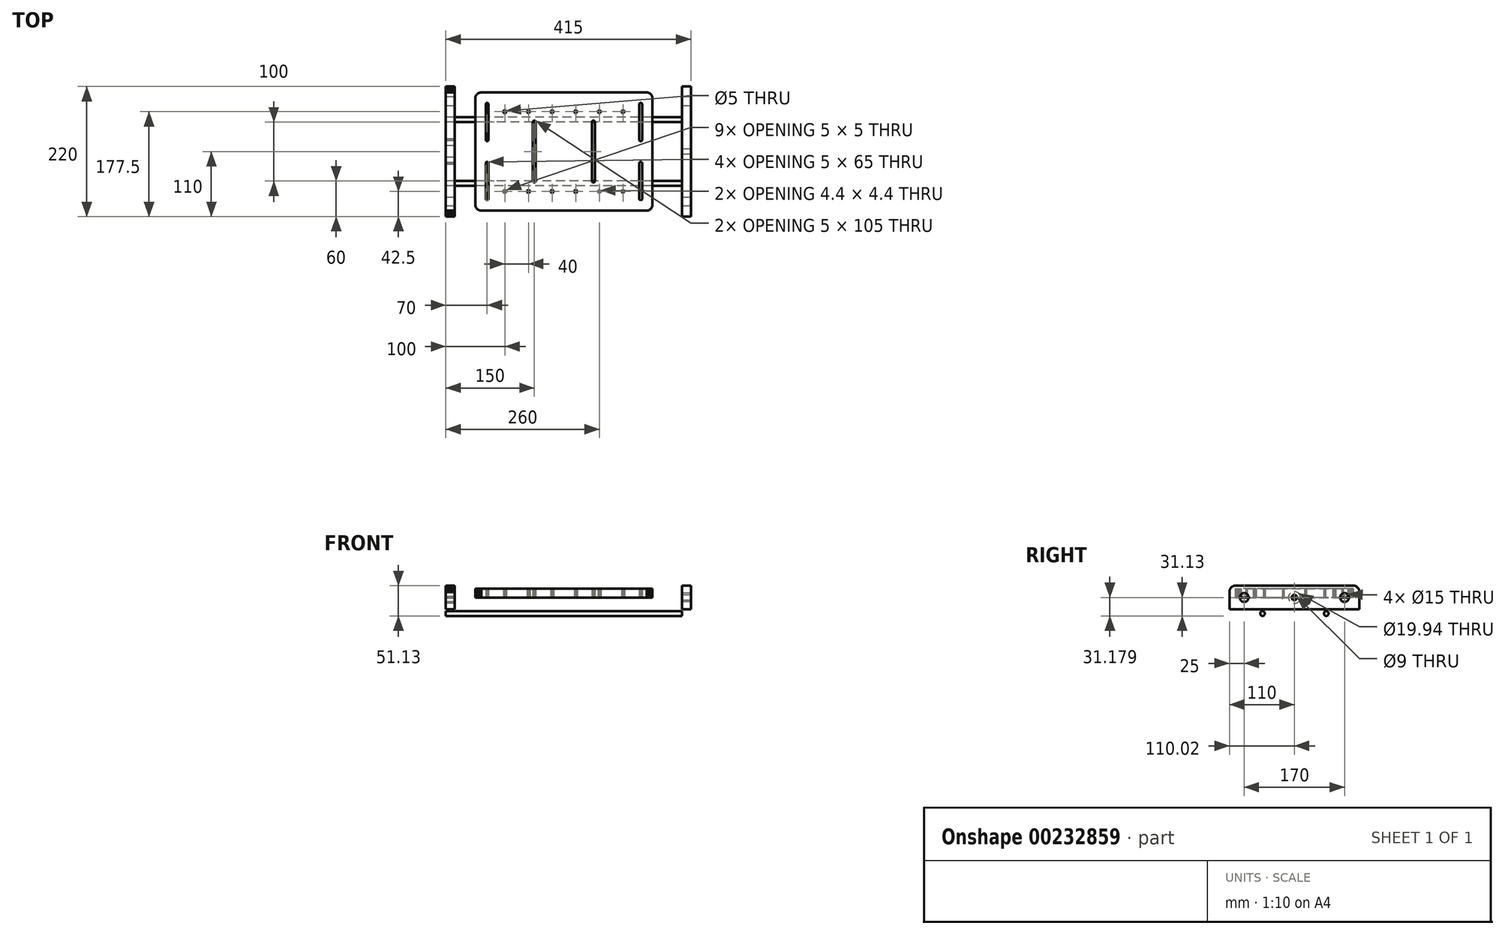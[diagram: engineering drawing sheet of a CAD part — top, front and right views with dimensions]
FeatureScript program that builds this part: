
annotation { "Feature Type Name" : "Feature", "Feature Type Description" : "" }
export const myFeature = defineFeature(function(context is Context, id is Id, definition is map)
    precondition{}
    {
        {
            var Q0;
            Q0=qCreatedBy(makeId("Top.planeOp"),FACE);
            var sketch = newSketch(context, id + "F0", { "sketchPlane" : qUnion([Q0])});
            skLineSegment(sketch, "E0", {"start": v(98.75, 69.67) * mm, "end": v(99.35, 69.91) * mm});
            skLineSegment(sketch, "E1", {"start": v(99.35, 69.91) * mm, "end": v(100, 70) * mm});
            skLineSegment(sketch, "E2", {"start": v(100, 70) * mm, "end": v(100.65, 69.91) * mm});
            skLineSegment(sketch, "E3", {"start": v(100.65, 69.91) * mm, "end": v(101.25, 69.67) * mm});
            skLineSegment(sketch, "E4", {"start": v(101.25, 69.67) * mm, "end": v(101.77, 69.27) * mm});
            skLineSegment(sketch, "E5", {"start": v(101.77, 69.27) * mm, "end": v(102.17, 68.75) * mm});
            skLineSegment(sketch, "E6", {"start": v(102.17, 68.75) * mm, "end": v(102.41, 68.15) * mm});
            skLineSegment(sketch, "E7", {"start": v(102.41, 68.15) * mm, "end": v(102.5, 67.5) * mm});
            skLineSegment(sketch, "E8", {"start": v(102.5, 67.5) * mm, "end": v(102.41, 66.85) * mm});
            skLineSegment(sketch, "E9", {"start": v(102.41, 66.85) * mm, "end": v(102.17, 66.25) * mm});
            skLineSegment(sketch, "E10", {"start": v(102.17, 66.25) * mm, "end": v(101.77, 65.73) * mm});
            skLineSegment(sketch, "E11", {"start": v(101.77, 65.73) * mm, "end": v(101.25, 65.33) * mm});
            skLineSegment(sketch, "E12", {"start": v(101.25, 65.33) * mm, "end": v(100.65, 65.09) * mm});
            skLineSegment(sketch, "E13", {"start": v(100.65, 65.09) * mm, "end": v(100, 65) * mm});
            skLineSegment(sketch, "E14", {"start": v(100, 65) * mm, "end": v(99.35, 65.09) * mm});
            skLineSegment(sketch, "E15", {"start": v(99.35, 65.09) * mm, "end": v(98.75, 65.33) * mm});
            skLineSegment(sketch, "E16", {"start": v(98.75, 65.33) * mm, "end": v(98.23, 65.73) * mm});
            skLineSegment(sketch, "E17", {"start": v(98.23, 65.73) * mm, "end": v(97.83, 66.25) * mm});
            skLineSegment(sketch, "E18", {"start": v(97.83, 66.25) * mm, "end": v(97.59, 66.85) * mm});
            skLineSegment(sketch, "E19", {"start": v(97.59, 66.85) * mm, "end": v(97.5, 67.5) * mm});
            skLineSegment(sketch, "E20", {"start": v(97.5, 67.5) * mm, "end": v(97.59, 68.15) * mm});
            skLineSegment(sketch, "E21", {"start": v(97.59, 68.15) * mm, "end": v(97.83, 68.75) * mm});
            skLineSegment(sketch, "E22", {"start": v(97.83, 68.75) * mm, "end": v(98.23, 69.27) * mm});
            skLineSegment(sketch, "E23", {"start": v(98.23, 69.27) * mm, "end": v(98.75, 69.67) * mm});
            skLineSegment(sketch, "E24", {"start": v(98.55, 67.89) * mm, "end": v(98.5, 67.5) * mm});
            skLineSegment(sketch, "E25", {"start": v(98.5, 67.5) * mm, "end": v(98.55, 67.11) * mm});
            skLineSegment(sketch, "E26", {"start": v(98.55, 67.11) * mm, "end": v(98.7, 66.75) * mm});
            skLineSegment(sketch, "E27", {"start": v(98.7, 66.75) * mm, "end": v(98.94, 66.44) * mm});
            skLineSegment(sketch, "E28", {"start": v(98.94, 66.44) * mm, "end": v(99.25, 66.2) * mm});
            skLineSegment(sketch, "E29", {"start": v(99.25, 66.2) * mm, "end": v(99.61, 66.05) * mm});
            skLineSegment(sketch, "E30", {"start": v(99.61, 66.05) * mm, "end": v(100, 66) * mm});
            skLineSegment(sketch, "E31", {"start": v(100, 66) * mm, "end": v(100.39, 66.05) * mm});
            skLineSegment(sketch, "E32", {"start": v(100.39, 66.05) * mm, "end": v(100.75, 66.2) * mm});
            skLineSegment(sketch, "E33", {"start": v(100.75, 66.2) * mm, "end": v(101.06, 66.44) * mm});
            skLineSegment(sketch, "E34", {"start": v(101.06, 66.44) * mm, "end": v(101.3, 66.75) * mm});
            skLineSegment(sketch, "E35", {"start": v(101.3, 66.75) * mm, "end": v(101.45, 67.11) * mm});
            skLineSegment(sketch, "E36", {"start": v(101.45, 67.11) * mm, "end": v(101.5, 67.5) * mm});
            skLineSegment(sketch, "E37", {"start": v(101.5, 67.5) * mm, "end": v(101.45, 67.89) * mm});
            skLineSegment(sketch, "E38", {"start": v(101.45, 67.89) * mm, "end": v(101.3, 68.25) * mm});
            skLineSegment(sketch, "E39", {"start": v(101.3, 68.25) * mm, "end": v(101.06, 68.56) * mm});
            skLineSegment(sketch, "E40", {"start": v(101.06, 68.56) * mm, "end": v(100.75, 68.8) * mm});
            skLineSegment(sketch, "E41", {"start": v(100.75, 68.8) * mm, "end": v(100.39, 68.95) * mm});
            skLineSegment(sketch, "E42", {"start": v(100.39, 68.95) * mm, "end": v(100, 69) * mm});
            skLineSegment(sketch, "E43", {"start": v(100, 69) * mm, "end": v(99.61, 68.95) * mm});
            skLineSegment(sketch, "E44", {"start": v(99.61, 68.95) * mm, "end": v(99.25, 68.8) * mm});
            skLineSegment(sketch, "E45", {"start": v(99.25, 68.8) * mm, "end": v(98.94, 68.56) * mm});
            skLineSegment(sketch, "E46", {"start": v(98.94, 68.56) * mm, "end": v(98.7, 68.25) * mm});
            skLineSegment(sketch, "E47", {"start": v(98.7, 68.25) * mm, "end": v(98.55, 67.89) * mm});
            skLineSegment(sketch, "E48", {"start": v(-101.25, -69.67) * mm, "end": v(-101.77, -69.27) * mm});
            skLineSegment(sketch, "E49", {"start": v(-101.77, -69.27) * mm, "end": v(-102.17, -68.75) * mm});
            skLineSegment(sketch, "E50", {"start": v(-102.17, -68.75) * mm, "end": v(-102.41, -68.15) * mm});
            skLineSegment(sketch, "E51", {"start": v(-102.41, -68.15) * mm, "end": v(-102.5, -67.5) * mm});
            skLineSegment(sketch, "E52", {"start": v(-102.5, -67.5) * mm, "end": v(-102.41, -66.85) * mm});
            skLineSegment(sketch, "E53", {"start": v(-102.41, -66.85) * mm, "end": v(-102.17, -66.25) * mm});
            skLineSegment(sketch, "E54", {"start": v(-102.17, -66.25) * mm, "end": v(-101.77, -65.73) * mm});
            skLineSegment(sketch, "E55", {"start": v(-101.77, -65.73) * mm, "end": v(-101.25, -65.33) * mm});
            skLineSegment(sketch, "E56", {"start": v(-101.25, -65.33) * mm, "end": v(-100.65, -65.09) * mm});
            skLineSegment(sketch, "E57", {"start": v(-100.65, -65.09) * mm, "end": v(-100, -65) * mm});
            skLineSegment(sketch, "E58", {"start": v(-100, -65) * mm, "end": v(-99.35, -65.09) * mm});
            skLineSegment(sketch, "E59", {"start": v(-99.35, -65.09) * mm, "end": v(-98.75, -65.33) * mm});
            skLineSegment(sketch, "E60", {"start": v(-98.75, -65.33) * mm, "end": v(-98.23, -65.73) * mm});
            skLineSegment(sketch, "E61", {"start": v(-98.23, -65.73) * mm, "end": v(-97.83, -66.25) * mm});
            skLineSegment(sketch, "E62", {"start": v(-97.83, -66.25) * mm, "end": v(-97.59, -66.85) * mm});
            skLineSegment(sketch, "E63", {"start": v(-97.59, -66.85) * mm, "end": v(-97.5, -67.5) * mm});
            skLineSegment(sketch, "E64", {"start": v(-97.5, -67.5) * mm, "end": v(-97.59, -68.15) * mm});
            skLineSegment(sketch, "E65", {"start": v(-97.59, -68.15) * mm, "end": v(-97.83, -68.75) * mm});
            skLineSegment(sketch, "E66", {"start": v(-97.83, -68.75) * mm, "end": v(-98.23, -69.27) * mm});
            skLineSegment(sketch, "E67", {"start": v(-98.23, -69.27) * mm, "end": v(-98.75, -69.67) * mm});
            skLineSegment(sketch, "E68", {"start": v(-98.75, -69.67) * mm, "end": v(-99.35, -69.91) * mm});
            skLineSegment(sketch, "E69", {"start": v(-99.35, -69.91) * mm, "end": v(-100, -70) * mm});
            skLineSegment(sketch, "E70", {"start": v(-100, -70) * mm, "end": v(-100.65, -69.91) * mm});
            skLineSegment(sketch, "E71", {"start": v(-100.65, -69.91) * mm, "end": v(-101.25, -69.67) * mm});
            skLineSegment(sketch, "E72", {"start": v(-101.45, -67.89) * mm, "end": v(-101.3, -68.25) * mm});
            skLineSegment(sketch, "E73", {"start": v(-101.3, -68.25) * mm, "end": v(-101.06, -68.56) * mm});
            skLineSegment(sketch, "E74", {"start": v(-101.06, -68.56) * mm, "end": v(-100.75, -68.8) * mm});
            skLineSegment(sketch, "E75", {"start": v(-100.75, -68.8) * mm, "end": v(-100.39, -68.95) * mm});
            skLineSegment(sketch, "E76", {"start": v(-100.39, -68.95) * mm, "end": v(-100, -69) * mm});
            skLineSegment(sketch, "E77", {"start": v(-100, -69) * mm, "end": v(-99.61, -68.95) * mm});
            skLineSegment(sketch, "E78", {"start": v(-99.61, -68.95) * mm, "end": v(-99.25, -68.8) * mm});
            skLineSegment(sketch, "E79", {"start": v(-99.25, -68.8) * mm, "end": v(-98.94, -68.56) * mm});
            skLineSegment(sketch, "E80", {"start": v(-98.94, -68.56) * mm, "end": v(-98.7, -68.25) * mm});
            skLineSegment(sketch, "E81", {"start": v(-98.7, -68.25) * mm, "end": v(-98.55, -67.89) * mm});
            skLineSegment(sketch, "E82", {"start": v(-98.55, -67.89) * mm, "end": v(-98.5, -67.5) * mm});
            skLineSegment(sketch, "E83", {"start": v(-98.5, -67.5) * mm, "end": v(-98.55, -67.11) * mm});
            skLineSegment(sketch, "E84", {"start": v(-98.55, -67.11) * mm, "end": v(-98.7, -66.75) * mm});
            skLineSegment(sketch, "E85", {"start": v(-98.7, -66.75) * mm, "end": v(-98.94, -66.44) * mm});
            skLineSegment(sketch, "E86", {"start": v(-98.94, -66.44) * mm, "end": v(-99.25, -66.2) * mm});
            skLineSegment(sketch, "E87", {"start": v(-99.25, -66.2) * mm, "end": v(-99.61, -66.05) * mm});
            skLineSegment(sketch, "E88", {"start": v(-99.61, -66.05) * mm, "end": v(-100, -66) * mm});
            skLineSegment(sketch, "E89", {"start": v(-100, -66) * mm, "end": v(-100.39, -66.05) * mm});
            skLineSegment(sketch, "E90", {"start": v(-100.39, -66.05) * mm, "end": v(-100.75, -66.2) * mm});
            skLineSegment(sketch, "E91", {"start": v(-100.75, -66.2) * mm, "end": v(-101.06, -66.44) * mm});
            skLineSegment(sketch, "E92", {"start": v(-101.06, -66.44) * mm, "end": v(-101.3, -66.75) * mm});
            skLineSegment(sketch, "E93", {"start": v(-101.3, -66.75) * mm, "end": v(-101.45, -67.11) * mm});
            skLineSegment(sketch, "E94", {"start": v(-101.45, -67.11) * mm, "end": v(-101.5, -67.5) * mm});
            skLineSegment(sketch, "E95", {"start": v(-101.5, -67.5) * mm, "end": v(-101.45, -67.89) * mm});
            skLineSegment(sketch, "E96", {"start": v(60, -65.3) * mm, "end": v(60.57, -65.37) * mm});
            skLineSegment(sketch, "E97", {"start": v(60.57, -65.37) * mm, "end": v(61.1, -65.6) * mm});
            skLineSegment(sketch, "E98", {"start": v(61.1, -65.6) * mm, "end": v(61.56, -65.94) * mm});
            skLineSegment(sketch, "E99", {"start": v(61.56, -65.94) * mm, "end": v(61.9, -66.4) * mm});
            skLineSegment(sketch, "E100", {"start": v(61.9, -66.4) * mm, "end": v(62.13, -66.93) * mm});
            skLineSegment(sketch, "E101", {"start": v(62.13, -66.93) * mm, "end": v(62.2, -67.5) * mm});
            skLineSegment(sketch, "E102", {"start": v(62.2, -67.5) * mm, "end": v(62.13, -68.07) * mm});
            skLineSegment(sketch, "E103", {"start": v(62.13, -68.07) * mm, "end": v(61.9, -68.6) * mm});
            skLineSegment(sketch, "E104", {"start": v(61.9, -68.6) * mm, "end": v(61.56, -69.06) * mm});
            skLineSegment(sketch, "E105", {"start": v(61.56, -69.06) * mm, "end": v(61.1, -69.4) * mm});
            skLineSegment(sketch, "E106", {"start": v(61.1, -69.4) * mm, "end": v(60.57, -69.63) * mm});
            skLineSegment(sketch, "E107", {"start": v(60.57, -69.63) * mm, "end": v(60, -69.7) * mm});
            skLineSegment(sketch, "E108", {"start": v(60, -69.7) * mm, "end": v(59.43, -69.63) * mm});
            skLineSegment(sketch, "E109", {"start": v(59.43, -69.63) * mm, "end": v(58.9, -69.4) * mm});
            skLineSegment(sketch, "E110", {"start": v(58.9, -69.4) * mm, "end": v(58.44, -69.06) * mm});
            skLineSegment(sketch, "E111", {"start": v(58.44, -69.06) * mm, "end": v(58.1, -68.6) * mm});
            skLineSegment(sketch, "E112", {"start": v(58.1, -68.6) * mm, "end": v(57.87, -68.07) * mm});
            skLineSegment(sketch, "E113", {"start": v(57.87, -68.07) * mm, "end": v(57.8, -67.5) * mm});
            skLineSegment(sketch, "E114", {"start": v(57.8, -67.5) * mm, "end": v(57.87, -66.93) * mm});
            skLineSegment(sketch, "E115", {"start": v(57.87, -66.93) * mm, "end": v(58.1, -66.4) * mm});
            skLineSegment(sketch, "E116", {"start": v(58.1, -66.4) * mm, "end": v(58.44, -65.94) * mm});
            skLineSegment(sketch, "E117", {"start": v(58.44, -65.94) * mm, "end": v(58.9, -65.6) * mm});
            skLineSegment(sketch, "E118", {"start": v(58.9, -65.6) * mm, "end": v(59.43, -65.37) * mm});
            skLineSegment(sketch, "E119", {"start": v(59.43, -65.37) * mm, "end": v(60, -65.3) * mm});
            skLineSegment(sketch, "E120", {"start": v(61.3, -66.75) * mm, "end": v(61.06, -66.44) * mm});
            skLineSegment(sketch, "E121", {"start": v(61.06, -66.44) * mm, "end": v(60.75, -66.2) * mm});
            skLineSegment(sketch, "E122", {"start": v(60.75, -66.2) * mm, "end": v(60.39, -66.05) * mm});
            skLineSegment(sketch, "E123", {"start": v(60.39, -66.05) * mm, "end": v(60, -66) * mm});
            skLineSegment(sketch, "E124", {"start": v(60, -66) * mm, "end": v(59.61, -66.05) * mm});
            skLineSegment(sketch, "E125", {"start": v(59.61, -66.05) * mm, "end": v(59.25, -66.2) * mm});
            skLineSegment(sketch, "E126", {"start": v(59.25, -66.2) * mm, "end": v(58.94, -66.44) * mm});
            skLineSegment(sketch, "E127", {"start": v(58.94, -66.44) * mm, "end": v(58.7, -66.75) * mm});
            skLineSegment(sketch, "E128", {"start": v(58.7, -66.75) * mm, "end": v(58.55, -67.11) * mm});
            skLineSegment(sketch, "E129", {"start": v(58.55, -67.11) * mm, "end": v(58.5, -67.5) * mm});
            skLineSegment(sketch, "E130", {"start": v(58.5, -67.5) * mm, "end": v(58.55, -67.89) * mm});
            skLineSegment(sketch, "E131", {"start": v(58.55, -67.89) * mm, "end": v(58.7, -68.25) * mm});
            skLineSegment(sketch, "E132", {"start": v(58.7, -68.25) * mm, "end": v(58.94, -68.56) * mm});
            skLineSegment(sketch, "E133", {"start": v(58.94, -68.56) * mm, "end": v(59.25, -68.8) * mm});
            skLineSegment(sketch, "E134", {"start": v(59.25, -68.8) * mm, "end": v(59.61, -68.95) * mm});
            skLineSegment(sketch, "E135", {"start": v(59.61, -68.95) * mm, "end": v(60, -69) * mm});
            skLineSegment(sketch, "E136", {"start": v(60, -69) * mm, "end": v(60.39, -68.95) * mm});
            skLineSegment(sketch, "E137", {"start": v(60.39, -68.95) * mm, "end": v(60.75, -68.8) * mm});
            skLineSegment(sketch, "E138", {"start": v(60.75, -68.8) * mm, "end": v(61.06, -68.56) * mm});
            skLineSegment(sketch, "E139", {"start": v(61.06, -68.56) * mm, "end": v(61.3, -68.25) * mm});
            skLineSegment(sketch, "E140", {"start": v(61.3, -68.25) * mm, "end": v(61.45, -67.89) * mm});
            skLineSegment(sketch, "E141", {"start": v(61.45, -67.89) * mm, "end": v(61.5, -67.5) * mm});
            skLineSegment(sketch, "E142", {"start": v(61.5, -67.5) * mm, "end": v(61.45, -67.11) * mm});
            skLineSegment(sketch, "E143", {"start": v(61.45, -67.11) * mm, "end": v(61.3, -66.75) * mm});
            skLineSegment(sketch, "E144", {"start": v(-18.23, -65.73) * mm, "end": v(-17.83, -66.25) * mm});
            skLineSegment(sketch, "E145", {"start": v(-17.83, -66.25) * mm, "end": v(-17.59, -66.85) * mm});
            skLineSegment(sketch, "E146", {"start": v(-17.59, -66.85) * mm, "end": v(-17.5, -67.5) * mm});
            skLineSegment(sketch, "E147", {"start": v(-17.5, -67.5) * mm, "end": v(-17.59, -68.15) * mm});
            skLineSegment(sketch, "E148", {"start": v(-17.59, -68.15) * mm, "end": v(-17.83, -68.75) * mm});
            skLineSegment(sketch, "E149", {"start": v(-17.83, -68.75) * mm, "end": v(-18.23, -69.27) * mm});
            skLineSegment(sketch, "E150", {"start": v(-18.23, -69.27) * mm, "end": v(-18.75, -69.67) * mm});
            skLineSegment(sketch, "E151", {"start": v(-18.75, -69.67) * mm, "end": v(-19.35, -69.91) * mm});
            skLineSegment(sketch, "E152", {"start": v(-19.35, -69.91) * mm, "end": v(-20, -70) * mm});
            skLineSegment(sketch, "E153", {"start": v(-20, -70) * mm, "end": v(-20.65, -69.91) * mm});
            skLineSegment(sketch, "E154", {"start": v(-20.65, -69.91) * mm, "end": v(-21.25, -69.67) * mm});
            skLineSegment(sketch, "E155", {"start": v(-21.25, -69.67) * mm, "end": v(-21.77, -69.27) * mm});
            skLineSegment(sketch, "E156", {"start": v(-21.77, -69.27) * mm, "end": v(-22.17, -68.75) * mm});
            skLineSegment(sketch, "E157", {"start": v(-22.17, -68.75) * mm, "end": v(-22.41, -68.15) * mm});
            skLineSegment(sketch, "E158", {"start": v(-22.41, -68.15) * mm, "end": v(-22.5, -67.5) * mm});
            skLineSegment(sketch, "E159", {"start": v(-22.5, -67.5) * mm, "end": v(-22.41, -66.85) * mm});
            skLineSegment(sketch, "E160", {"start": v(-22.41, -66.85) * mm, "end": v(-22.17, -66.25) * mm});
            skLineSegment(sketch, "E161", {"start": v(-22.17, -66.25) * mm, "end": v(-21.77, -65.73) * mm});
            skLineSegment(sketch, "E162", {"start": v(-21.77, -65.73) * mm, "end": v(-21.25, -65.33) * mm});
            skLineSegment(sketch, "E163", {"start": v(-21.25, -65.33) * mm, "end": v(-20.65, -65.09) * mm});
            skLineSegment(sketch, "E164", {"start": v(-20.65, -65.09) * mm, "end": v(-20, -65) * mm});
            skLineSegment(sketch, "E165", {"start": v(-20, -65) * mm, "end": v(-19.35, -65.09) * mm});
            skLineSegment(sketch, "E166", {"start": v(-19.35, -65.09) * mm, "end": v(-18.75, -65.33) * mm});
            skLineSegment(sketch, "E167", {"start": v(-18.75, -65.33) * mm, "end": v(-18.23, -65.73) * mm});
            skLineSegment(sketch, "E168", {"start": v(-20.39, -68.95) * mm, "end": v(-20, -69) * mm});
            skLineSegment(sketch, "E169", {"start": v(-20, -69) * mm, "end": v(-19.61, -68.95) * mm});
            skLineSegment(sketch, "E170", {"start": v(-19.61, -68.95) * mm, "end": v(-19.25, -68.8) * mm});
            skLineSegment(sketch, "E171", {"start": v(-19.25, -68.8) * mm, "end": v(-18.94, -68.56) * mm});
            skLineSegment(sketch, "E172", {"start": v(-18.94, -68.56) * mm, "end": v(-18.7, -68.25) * mm});
            skLineSegment(sketch, "E173", {"start": v(-18.7, -68.25) * mm, "end": v(-18.55, -67.89) * mm});
            skLineSegment(sketch, "E174", {"start": v(-18.55, -67.89) * mm, "end": v(-18.5, -67.5) * mm});
            skLineSegment(sketch, "E175", {"start": v(-18.5, -67.5) * mm, "end": v(-18.55, -67.11) * mm});
            skLineSegment(sketch, "E176", {"start": v(-18.55, -67.11) * mm, "end": v(-18.7, -66.75) * mm});
            skLineSegment(sketch, "E177", {"start": v(-18.7, -66.75) * mm, "end": v(-18.94, -66.44) * mm});
            skLineSegment(sketch, "E178", {"start": v(-18.94, -66.44) * mm, "end": v(-19.25, -66.2) * mm});
            skLineSegment(sketch, "E179", {"start": v(-19.25, -66.2) * mm, "end": v(-19.61, -66.05) * mm});
            skLineSegment(sketch, "E180", {"start": v(-19.61, -66.05) * mm, "end": v(-20, -66) * mm});
            skLineSegment(sketch, "E181", {"start": v(-20, -66) * mm, "end": v(-20.39, -66.05) * mm});
            skLineSegment(sketch, "E182", {"start": v(-20.39, -66.05) * mm, "end": v(-20.75, -66.2) * mm});
            skLineSegment(sketch, "E183", {"start": v(-20.75, -66.2) * mm, "end": v(-21.06, -66.44) * mm});
            skLineSegment(sketch, "E184", {"start": v(-21.06, -66.44) * mm, "end": v(-21.3, -66.75) * mm});
            skLineSegment(sketch, "E185", {"start": v(-21.3, -66.75) * mm, "end": v(-21.45, -67.11) * mm});
            skLineSegment(sketch, "E186", {"start": v(-21.45, -67.11) * mm, "end": v(-21.5, -67.5) * mm});
            skLineSegment(sketch, "E187", {"start": v(-21.5, -67.5) * mm, "end": v(-21.45, -67.89) * mm});
            skLineSegment(sketch, "E188", {"start": v(-21.45, -67.89) * mm, "end": v(-21.3, -68.25) * mm});
            skLineSegment(sketch, "E189", {"start": v(-21.3, -68.25) * mm, "end": v(-21.06, -68.56) * mm});
            skLineSegment(sketch, "E190", {"start": v(-21.06, -68.56) * mm, "end": v(-20.75, -68.8) * mm});
            skLineSegment(sketch, "E191", {"start": v(-20.75, -68.8) * mm, "end": v(-20.39, -68.95) * mm});
            skLineSegment(sketch, "E192", {"start": v(21.25, 65.33) * mm, "end": v(20.65, 65.09) * mm});
            skLineSegment(sketch, "E193", {"start": v(20.65, 65.09) * mm, "end": v(20, 65) * mm});
            skLineSegment(sketch, "E194", {"start": v(20, 65) * mm, "end": v(19.35, 65.09) * mm});
            skLineSegment(sketch, "E195", {"start": v(19.35, 65.09) * mm, "end": v(18.75, 65.33) * mm});
            skLineSegment(sketch, "E196", {"start": v(18.75, 65.33) * mm, "end": v(18.23, 65.73) * mm});
            skLineSegment(sketch, "E197", {"start": v(18.23, 65.73) * mm, "end": v(17.83, 66.25) * mm});
            skLineSegment(sketch, "E198", {"start": v(17.83, 66.25) * mm, "end": v(17.59, 66.85) * mm});
            skLineSegment(sketch, "E199", {"start": v(17.59, 66.85) * mm, "end": v(17.5, 67.5) * mm});
            skLineSegment(sketch, "E200", {"start": v(17.5, 67.5) * mm, "end": v(17.59, 68.15) * mm});
            skLineSegment(sketch, "E201", {"start": v(17.59, 68.15) * mm, "end": v(17.83, 68.75) * mm});
            skLineSegment(sketch, "E202", {"start": v(17.83, 68.75) * mm, "end": v(18.23, 69.27) * mm});
            skLineSegment(sketch, "E203", {"start": v(18.23, 69.27) * mm, "end": v(18.75, 69.67) * mm});
            skLineSegment(sketch, "E204", {"start": v(18.75, 69.67) * mm, "end": v(19.35, 69.91) * mm});
            skLineSegment(sketch, "E205", {"start": v(19.35, 69.91) * mm, "end": v(20, 70) * mm});
            skLineSegment(sketch, "E206", {"start": v(20, 70) * mm, "end": v(20.65, 69.91) * mm});
            skLineSegment(sketch, "E207", {"start": v(20.65, 69.91) * mm, "end": v(21.25, 69.67) * mm});
            skLineSegment(sketch, "E208", {"start": v(21.25, 69.67) * mm, "end": v(21.77, 69.27) * mm});
            skLineSegment(sketch, "E209", {"start": v(21.77, 69.27) * mm, "end": v(22.17, 68.75) * mm});
            skLineSegment(sketch, "E210", {"start": v(22.17, 68.75) * mm, "end": v(22.41, 68.15) * mm});
            skLineSegment(sketch, "E211", {"start": v(22.41, 68.15) * mm, "end": v(22.5, 67.5) * mm});
            skLineSegment(sketch, "E212", {"start": v(22.5, 67.5) * mm, "end": v(22.41, 66.85) * mm});
            skLineSegment(sketch, "E213", {"start": v(22.41, 66.85) * mm, "end": v(22.17, 66.25) * mm});
            skLineSegment(sketch, "E214", {"start": v(22.17, 66.25) * mm, "end": v(21.77, 65.73) * mm});
            skLineSegment(sketch, "E215", {"start": v(21.77, 65.73) * mm, "end": v(21.25, 65.33) * mm});
            skLineSegment(sketch, "E216", {"start": v(20, 66) * mm, "end": v(20.39, 66.05) * mm});
            skLineSegment(sketch, "E217", {"start": v(20.39, 66.05) * mm, "end": v(20.75, 66.2) * mm});
            skLineSegment(sketch, "E218", {"start": v(20.75, 66.2) * mm, "end": v(21.06, 66.44) * mm});
            skLineSegment(sketch, "E219", {"start": v(21.06, 66.44) * mm, "end": v(21.3, 66.75) * mm});
            skLineSegment(sketch, "E220", {"start": v(21.3, 66.75) * mm, "end": v(21.45, 67.11) * mm});
            skLineSegment(sketch, "E221", {"start": v(21.45, 67.11) * mm, "end": v(21.5, 67.5) * mm});
            skLineSegment(sketch, "E222", {"start": v(21.5, 67.5) * mm, "end": v(21.45, 67.89) * mm});
            skLineSegment(sketch, "E223", {"start": v(21.45, 67.89) * mm, "end": v(21.3, 68.25) * mm});
            skLineSegment(sketch, "E224", {"start": v(21.3, 68.25) * mm, "end": v(21.06, 68.56) * mm});
            skLineSegment(sketch, "E225", {"start": v(21.06, 68.56) * mm, "end": v(20.75, 68.8) * mm});
            skLineSegment(sketch, "E226", {"start": v(20.75, 68.8) * mm, "end": v(20.39, 68.95) * mm});
            skLineSegment(sketch, "E227", {"start": v(20.39, 68.95) * mm, "end": v(20, 69) * mm});
            skLineSegment(sketch, "E228", {"start": v(20, 69) * mm, "end": v(19.61, 68.95) * mm});
            skLineSegment(sketch, "E229", {"start": v(19.61, 68.95) * mm, "end": v(19.25, 68.8) * mm});
            skLineSegment(sketch, "E230", {"start": v(19.25, 68.8) * mm, "end": v(18.94, 68.56) * mm});
            skLineSegment(sketch, "E231", {"start": v(18.94, 68.56) * mm, "end": v(18.7, 68.25) * mm});
            skLineSegment(sketch, "E232", {"start": v(18.7, 68.25) * mm, "end": v(18.55, 67.89) * mm});
            skLineSegment(sketch, "E233", {"start": v(18.55, 67.89) * mm, "end": v(18.5, 67.5) * mm});
            skLineSegment(sketch, "E234", {"start": v(18.5, 67.5) * mm, "end": v(18.55, 67.11) * mm});
            skLineSegment(sketch, "E235", {"start": v(18.55, 67.11) * mm, "end": v(18.7, 66.75) * mm});
            skLineSegment(sketch, "E236", {"start": v(18.7, 66.75) * mm, "end": v(18.94, 66.44) * mm});
            skLineSegment(sketch, "E237", {"start": v(18.94, 66.44) * mm, "end": v(19.25, 66.2) * mm});
            skLineSegment(sketch, "E238", {"start": v(19.25, 66.2) * mm, "end": v(19.61, 66.05) * mm});
            skLineSegment(sketch, "E239", {"start": v(19.61, 66.05) * mm, "end": v(20, 66) * mm});
            skLineSegment(sketch, "E240", {"start": v(17.83, -66.25) * mm, "end": v(18.23, -65.73) * mm});
            skLineSegment(sketch, "E241", {"start": v(18.23, -65.73) * mm, "end": v(18.75, -65.33) * mm});
            skLineSegment(sketch, "E242", {"start": v(18.75, -65.33) * mm, "end": v(19.35, -65.09) * mm});
            skLineSegment(sketch, "E243", {"start": v(19.35, -65.09) * mm, "end": v(20, -65) * mm});
            skLineSegment(sketch, "E244", {"start": v(20, -65) * mm, "end": v(20.65, -65.09) * mm});
            skLineSegment(sketch, "E245", {"start": v(20.65, -65.09) * mm, "end": v(21.25, -65.33) * mm});
            skLineSegment(sketch, "E246", {"start": v(21.25, -65.33) * mm, "end": v(21.77, -65.73) * mm});
            skLineSegment(sketch, "E247", {"start": v(21.77, -65.73) * mm, "end": v(22.17, -66.25) * mm});
            skLineSegment(sketch, "E248", {"start": v(22.17, -66.25) * mm, "end": v(22.41, -66.85) * mm});
            skLineSegment(sketch, "E249", {"start": v(22.41, -66.85) * mm, "end": v(22.5, -67.5) * mm});
            skLineSegment(sketch, "E250", {"start": v(22.5, -67.5) * mm, "end": v(22.41, -68.15) * mm});
            skLineSegment(sketch, "E251", {"start": v(22.41, -68.15) * mm, "end": v(22.17, -68.75) * mm});
            skLineSegment(sketch, "E252", {"start": v(22.17, -68.75) * mm, "end": v(21.77, -69.27) * mm});
            skLineSegment(sketch, "E253", {"start": v(21.77, -69.27) * mm, "end": v(21.25, -69.67) * mm});
            skLineSegment(sketch, "E254", {"start": v(21.25, -69.67) * mm, "end": v(20.65, -69.91) * mm});
            skLineSegment(sketch, "E255", {"start": v(20.65, -69.91) * mm, "end": v(20, -70) * mm});
            skLineSegment(sketch, "E256", {"start": v(20, -70) * mm, "end": v(19.35, -69.91) * mm});
            skLineSegment(sketch, "E257", {"start": v(19.35, -69.91) * mm, "end": v(18.75, -69.67) * mm});
            skLineSegment(sketch, "E258", {"start": v(18.75, -69.67) * mm, "end": v(18.23, -69.27) * mm});
            skLineSegment(sketch, "E259", {"start": v(18.23, -69.27) * mm, "end": v(17.83, -68.75) * mm});
            skLineSegment(sketch, "E260", {"start": v(17.83, -68.75) * mm, "end": v(17.59, -68.15) * mm});
            skLineSegment(sketch, "E261", {"start": v(17.59, -68.15) * mm, "end": v(17.5, -67.5) * mm});
            skLineSegment(sketch, "E262", {"start": v(17.5, -67.5) * mm, "end": v(17.59, -66.85) * mm});
            skLineSegment(sketch, "E263", {"start": v(17.59, -66.85) * mm, "end": v(17.83, -66.25) * mm});
            skLineSegment(sketch, "E264", {"start": v(21.45, -67.89) * mm, "end": v(21.5, -67.5) * mm});
            skLineSegment(sketch, "E265", {"start": v(21.5, -67.5) * mm, "end": v(21.45, -67.11) * mm});
            skLineSegment(sketch, "E266", {"start": v(21.45, -67.11) * mm, "end": v(21.3, -66.75) * mm});
            skLineSegment(sketch, "E267", {"start": v(21.3, -66.75) * mm, "end": v(21.06, -66.44) * mm});
            skLineSegment(sketch, "E268", {"start": v(21.06, -66.44) * mm, "end": v(20.75, -66.2) * mm});
            skLineSegment(sketch, "E269", {"start": v(20.75, -66.2) * mm, "end": v(20.39, -66.05) * mm});
            skLineSegment(sketch, "E270", {"start": v(20.39, -66.05) * mm, "end": v(20, -66) * mm});
            skLineSegment(sketch, "E271", {"start": v(20, -66) * mm, "end": v(19.61, -66.05) * mm});
            skLineSegment(sketch, "E272", {"start": v(19.61, -66.05) * mm, "end": v(19.25, -66.2) * mm});
            skLineSegment(sketch, "E273", {"start": v(19.25, -66.2) * mm, "end": v(18.94, -66.44) * mm});
            skLineSegment(sketch, "E274", {"start": v(18.94, -66.44) * mm, "end": v(18.7, -66.75) * mm});
            skLineSegment(sketch, "E275", {"start": v(18.7, -66.75) * mm, "end": v(18.55, -67.11) * mm});
            skLineSegment(sketch, "E276", {"start": v(18.55, -67.11) * mm, "end": v(18.5, -67.5) * mm});
            skLineSegment(sketch, "E277", {"start": v(18.5, -67.5) * mm, "end": v(18.55, -67.89) * mm});
            skLineSegment(sketch, "E278", {"start": v(18.55, -67.89) * mm, "end": v(18.7, -68.25) * mm});
            skLineSegment(sketch, "E279", {"start": v(18.7, -68.25) * mm, "end": v(18.94, -68.56) * mm});
            skLineSegment(sketch, "E280", {"start": v(18.94, -68.56) * mm, "end": v(19.25, -68.8) * mm});
            skLineSegment(sketch, "E281", {"start": v(19.25, -68.8) * mm, "end": v(19.61, -68.95) * mm});
            skLineSegment(sketch, "E282", {"start": v(19.61, -68.95) * mm, "end": v(20, -69) * mm});
            skLineSegment(sketch, "E283", {"start": v(20, -69) * mm, "end": v(20.39, -68.95) * mm});
            skLineSegment(sketch, "E284", {"start": v(20.39, -68.95) * mm, "end": v(20.75, -68.8) * mm});
            skLineSegment(sketch, "E285", {"start": v(20.75, -68.8) * mm, "end": v(21.06, -68.56) * mm});
            skLineSegment(sketch, "E286", {"start": v(21.06, -68.56) * mm, "end": v(21.3, -68.25) * mm});
            skLineSegment(sketch, "E287", {"start": v(21.3, -68.25) * mm, "end": v(21.45, -67.89) * mm});
            skLineSegment(sketch, "E288", {"start": v(-20, 65) * mm, "end": v(-20.65, 65.09) * mm});
            skLineSegment(sketch, "E289", {"start": v(-20.65, 65.09) * mm, "end": v(-21.25, 65.33) * mm});
            skLineSegment(sketch, "E290", {"start": v(-21.25, 65.33) * mm, "end": v(-21.77, 65.73) * mm});
            skLineSegment(sketch, "E291", {"start": v(-21.77, 65.73) * mm, "end": v(-22.17, 66.25) * mm});
            skLineSegment(sketch, "E292", {"start": v(-22.17, 66.25) * mm, "end": v(-22.41, 66.85) * mm});
            skLineSegment(sketch, "E293", {"start": v(-22.41, 66.85) * mm, "end": v(-22.5, 67.5) * mm});
            skLineSegment(sketch, "E294", {"start": v(-22.5, 67.5) * mm, "end": v(-22.41, 68.15) * mm});
            skLineSegment(sketch, "E295", {"start": v(-22.41, 68.15) * mm, "end": v(-22.17, 68.75) * mm});
            skLineSegment(sketch, "E296", {"start": v(-22.17, 68.75) * mm, "end": v(-21.77, 69.27) * mm});
            skLineSegment(sketch, "E297", {"start": v(-21.77, 69.27) * mm, "end": v(-21.25, 69.67) * mm});
            skLineSegment(sketch, "E298", {"start": v(-21.25, 69.67) * mm, "end": v(-20.65, 69.91) * mm});
            skLineSegment(sketch, "E299", {"start": v(-20.65, 69.91) * mm, "end": v(-20, 70) * mm});
            skLineSegment(sketch, "E300", {"start": v(-20, 70) * mm, "end": v(-19.35, 69.91) * mm});
            skLineSegment(sketch, "E301", {"start": v(-19.35, 69.91) * mm, "end": v(-18.75, 69.67) * mm});
            skLineSegment(sketch, "E302", {"start": v(-18.75, 69.67) * mm, "end": v(-18.23, 69.27) * mm});
            skLineSegment(sketch, "E303", {"start": v(-18.23, 69.27) * mm, "end": v(-17.83, 68.75) * mm});
            skLineSegment(sketch, "E304", {"start": v(-17.83, 68.75) * mm, "end": v(-17.59, 68.15) * mm});
            skLineSegment(sketch, "E305", {"start": v(-17.59, 68.15) * mm, "end": v(-17.5, 67.5) * mm});
            skLineSegment(sketch, "E306", {"start": v(-17.5, 67.5) * mm, "end": v(-17.59, 66.85) * mm});
            skLineSegment(sketch, "E307", {"start": v(-17.59, 66.85) * mm, "end": v(-17.83, 66.25) * mm});
            skLineSegment(sketch, "E308", {"start": v(-17.83, 66.25) * mm, "end": v(-18.23, 65.73) * mm});
            skLineSegment(sketch, "E309", {"start": v(-18.23, 65.73) * mm, "end": v(-18.75, 65.33) * mm});
            skLineSegment(sketch, "E310", {"start": v(-18.75, 65.33) * mm, "end": v(-19.35, 65.09) * mm});
            skLineSegment(sketch, "E311", {"start": v(-19.35, 65.09) * mm, "end": v(-20, 65) * mm});
            skLineSegment(sketch, "E312", {"start": v(-18.94, 68.56) * mm, "end": v(-19.25, 68.8) * mm});
            skLineSegment(sketch, "E313", {"start": v(-19.25, 68.8) * mm, "end": v(-19.61, 68.95) * mm});
            skLineSegment(sketch, "E314", {"start": v(-19.61, 68.95) * mm, "end": v(-20, 69) * mm});
            skLineSegment(sketch, "E315", {"start": v(-20, 69) * mm, "end": v(-20.39, 68.95) * mm});
            skLineSegment(sketch, "E316", {"start": v(-20.39, 68.95) * mm, "end": v(-20.75, 68.8) * mm});
            skLineSegment(sketch, "E317", {"start": v(-20.75, 68.8) * mm, "end": v(-21.06, 68.56) * mm});
            skLineSegment(sketch, "E318", {"start": v(-21.06, 68.56) * mm, "end": v(-21.3, 68.25) * mm});
            skLineSegment(sketch, "E319", {"start": v(-21.3, 68.25) * mm, "end": v(-21.45, 67.89) * mm});
            skLineSegment(sketch, "E320", {"start": v(-21.45, 67.89) * mm, "end": v(-21.5, 67.5) * mm});
            skLineSegment(sketch, "E321", {"start": v(-21.5, 67.5) * mm, "end": v(-21.45, 67.11) * mm});
            skLineSegment(sketch, "E322", {"start": v(-21.45, 67.11) * mm, "end": v(-21.3, 66.75) * mm});
            skLineSegment(sketch, "E323", {"start": v(-21.3, 66.75) * mm, "end": v(-21.06, 66.44) * mm});
            skLineSegment(sketch, "E324", {"start": v(-21.06, 66.44) * mm, "end": v(-20.75, 66.2) * mm});
            skLineSegment(sketch, "E325", {"start": v(-20.75, 66.2) * mm, "end": v(-20.39, 66.05) * mm});
            skLineSegment(sketch, "E326", {"start": v(-20.39, 66.05) * mm, "end": v(-20, 66) * mm});
            skLineSegment(sketch, "E327", {"start": v(-20, 66) * mm, "end": v(-19.61, 66.05) * mm});
            skLineSegment(sketch, "E328", {"start": v(-19.61, 66.05) * mm, "end": v(-19.25, 66.2) * mm});
            skLineSegment(sketch, "E329", {"start": v(-19.25, 66.2) * mm, "end": v(-18.94, 66.44) * mm});
            skLineSegment(sketch, "E330", {"start": v(-18.94, 66.44) * mm, "end": v(-18.7, 66.75) * mm});
            skLineSegment(sketch, "E331", {"start": v(-18.7, 66.75) * mm, "end": v(-18.55, 67.11) * mm});
            skLineSegment(sketch, "E332", {"start": v(-18.55, 67.11) * mm, "end": v(-18.5, 67.5) * mm});
            skLineSegment(sketch, "E333", {"start": v(-18.5, 67.5) * mm, "end": v(-18.55, 67.89) * mm});
            skLineSegment(sketch, "E334", {"start": v(-18.55, 67.89) * mm, "end": v(-18.7, 68.25) * mm});
            skLineSegment(sketch, "E335", {"start": v(-18.7, 68.25) * mm, "end": v(-18.94, 68.56) * mm});
            skLineSegment(sketch, "E336", {"start": v(60, 65) * mm, "end": v(59.35, 65.09) * mm});
            skLineSegment(sketch, "E337", {"start": v(59.35, 65.09) * mm, "end": v(58.75, 65.33) * mm});
            skLineSegment(sketch, "E338", {"start": v(58.75, 65.33) * mm, "end": v(58.23, 65.73) * mm});
            skLineSegment(sketch, "E339", {"start": v(58.23, 65.73) * mm, "end": v(57.83, 66.25) * mm});
            skLineSegment(sketch, "E340", {"start": v(57.83, 66.25) * mm, "end": v(57.59, 66.85) * mm});
            skLineSegment(sketch, "E341", {"start": v(57.59, 66.85) * mm, "end": v(57.5, 67.5) * mm});
            skLineSegment(sketch, "E342", {"start": v(57.5, 67.5) * mm, "end": v(57.59, 68.15) * mm});
            skLineSegment(sketch, "E343", {"start": v(57.59, 68.15) * mm, "end": v(57.83, 68.75) * mm});
            skLineSegment(sketch, "E344", {"start": v(57.83, 68.75) * mm, "end": v(58.23, 69.27) * mm});
            skLineSegment(sketch, "E345", {"start": v(58.23, 69.27) * mm, "end": v(58.75, 69.67) * mm});
            skLineSegment(sketch, "E346", {"start": v(58.75, 69.67) * mm, "end": v(59.35, 69.91) * mm});
            skLineSegment(sketch, "E347", {"start": v(59.35, 69.91) * mm, "end": v(60, 70) * mm});
            skLineSegment(sketch, "E348", {"start": v(60, 70) * mm, "end": v(60.65, 69.91) * mm});
            skLineSegment(sketch, "E349", {"start": v(60.65, 69.91) * mm, "end": v(61.25, 69.67) * mm});
            skLineSegment(sketch, "E350", {"start": v(61.25, 69.67) * mm, "end": v(61.77, 69.27) * mm});
            skLineSegment(sketch, "E351", {"start": v(61.77, 69.27) * mm, "end": v(62.17, 68.75) * mm});
            skLineSegment(sketch, "E352", {"start": v(62.17, 68.75) * mm, "end": v(62.41, 68.15) * mm});
            skLineSegment(sketch, "E353", {"start": v(62.41, 68.15) * mm, "end": v(62.5, 67.5) * mm});
            skLineSegment(sketch, "E354", {"start": v(62.5, 67.5) * mm, "end": v(62.41, 66.85) * mm});
            skLineSegment(sketch, "E355", {"start": v(62.41, 66.85) * mm, "end": v(62.17, 66.25) * mm});
            skLineSegment(sketch, "E356", {"start": v(62.17, 66.25) * mm, "end": v(61.77, 65.73) * mm});
            skLineSegment(sketch, "E357", {"start": v(61.77, 65.73) * mm, "end": v(61.25, 65.33) * mm});
            skLineSegment(sketch, "E358", {"start": v(61.25, 65.33) * mm, "end": v(60.65, 65.09) * mm});
            skLineSegment(sketch, "E359", {"start": v(60.65, 65.09) * mm, "end": v(60, 65) * mm});
            skLineSegment(sketch, "E360", {"start": v(58.55, 67.89) * mm, "end": v(58.5, 67.5) * mm});
            skLineSegment(sketch, "E361", {"start": v(58.5, 67.5) * mm, "end": v(58.55, 67.11) * mm});
            skLineSegment(sketch, "E362", {"start": v(58.55, 67.11) * mm, "end": v(58.7, 66.75) * mm});
            skLineSegment(sketch, "E363", {"start": v(58.7, 66.75) * mm, "end": v(58.94, 66.44) * mm});
            skLineSegment(sketch, "E364", {"start": v(58.94, 66.44) * mm, "end": v(59.25, 66.2) * mm});
            skLineSegment(sketch, "E365", {"start": v(59.25, 66.2) * mm, "end": v(59.61, 66.05) * mm});
            skLineSegment(sketch, "E366", {"start": v(59.61, 66.05) * mm, "end": v(60, 66) * mm});
            skLineSegment(sketch, "E367", {"start": v(60, 66) * mm, "end": v(60.39, 66.05) * mm});
            skLineSegment(sketch, "E368", {"start": v(60.39, 66.05) * mm, "end": v(60.75, 66.2) * mm});
            skLineSegment(sketch, "E369", {"start": v(60.75, 66.2) * mm, "end": v(61.06, 66.44) * mm});
            skLineSegment(sketch, "E370", {"start": v(61.06, 66.44) * mm, "end": v(61.3, 66.75) * mm});
            skLineSegment(sketch, "E371", {"start": v(61.3, 66.75) * mm, "end": v(61.45, 67.11) * mm});
            skLineSegment(sketch, "E372", {"start": v(61.45, 67.11) * mm, "end": v(61.5, 67.5) * mm});
            skLineSegment(sketch, "E373", {"start": v(61.5, 67.5) * mm, "end": v(61.45, 67.89) * mm});
            skLineSegment(sketch, "E374", {"start": v(61.45, 67.89) * mm, "end": v(61.3, 68.25) * mm});
            skLineSegment(sketch, "E375", {"start": v(61.3, 68.25) * mm, "end": v(61.06, 68.56) * mm});
            skLineSegment(sketch, "E376", {"start": v(61.06, 68.56) * mm, "end": v(60.75, 68.8) * mm});
            skLineSegment(sketch, "E377", {"start": v(60.75, 68.8) * mm, "end": v(60.39, 68.95) * mm});
            skLineSegment(sketch, "E378", {"start": v(60.39, 68.95) * mm, "end": v(60, 69) * mm});
            skLineSegment(sketch, "E379", {"start": v(60, 69) * mm, "end": v(59.61, 68.95) * mm});
            skLineSegment(sketch, "E380", {"start": v(59.61, 68.95) * mm, "end": v(59.25, 68.8) * mm});
            skLineSegment(sketch, "E381", {"start": v(59.25, 68.8) * mm, "end": v(58.94, 68.56) * mm});
            skLineSegment(sketch, "E382", {"start": v(58.94, 68.56) * mm, "end": v(58.7, 68.25) * mm});
            skLineSegment(sketch, "E383", {"start": v(58.7, 68.25) * mm, "end": v(58.55, 67.89) * mm});
            skLineSegment(sketch, "E384", {"start": v(-57.83, 68.75) * mm, "end": v(-57.59, 68.15) * mm});
            skLineSegment(sketch, "E385", {"start": v(-57.59, 68.15) * mm, "end": v(-57.5, 67.5) * mm});
            skLineSegment(sketch, "E386", {"start": v(-57.5, 67.5) * mm, "end": v(-57.59, 66.85) * mm});
            skLineSegment(sketch, "E387", {"start": v(-57.59, 66.85) * mm, "end": v(-57.83, 66.25) * mm});
            skLineSegment(sketch, "E388", {"start": v(-57.83, 66.25) * mm, "end": v(-58.23, 65.73) * mm});
            skLineSegment(sketch, "E389", {"start": v(-58.23, 65.73) * mm, "end": v(-58.75, 65.33) * mm});
            skLineSegment(sketch, "E390", {"start": v(-58.75, 65.33) * mm, "end": v(-59.35, 65.09) * mm});
            skLineSegment(sketch, "E391", {"start": v(-59.35, 65.09) * mm, "end": v(-60, 65) * mm});
            skLineSegment(sketch, "E392", {"start": v(-60, 65) * mm, "end": v(-60.65, 65.09) * mm});
            skLineSegment(sketch, "E393", {"start": v(-60.65, 65.09) * mm, "end": v(-61.25, 65.33) * mm});
            skLineSegment(sketch, "E394", {"start": v(-61.25, 65.33) * mm, "end": v(-61.77, 65.73) * mm});
            skLineSegment(sketch, "E395", {"start": v(-61.77, 65.73) * mm, "end": v(-62.17, 66.25) * mm});
            skLineSegment(sketch, "E396", {"start": v(-62.17, 66.25) * mm, "end": v(-62.41, 66.85) * mm});
            skLineSegment(sketch, "E397", {"start": v(-62.41, 66.85) * mm, "end": v(-62.5, 67.5) * mm});
            skLineSegment(sketch, "E398", {"start": v(-62.5, 67.5) * mm, "end": v(-62.41, 68.15) * mm});
            skLineSegment(sketch, "E399", {"start": v(-62.41, 68.15) * mm, "end": v(-62.17, 68.75) * mm});
            skLineSegment(sketch, "E400", {"start": v(-62.17, 68.75) * mm, "end": v(-61.77, 69.27) * mm});
            skLineSegment(sketch, "E401", {"start": v(-61.77, 69.27) * mm, "end": v(-61.25, 69.67) * mm});
            skLineSegment(sketch, "E402", {"start": v(-61.25, 69.67) * mm, "end": v(-60.65, 69.91) * mm});
            skLineSegment(sketch, "E403", {"start": v(-60.65, 69.91) * mm, "end": v(-60, 70) * mm});
            skLineSegment(sketch, "E404", {"start": v(-60, 70) * mm, "end": v(-59.35, 69.91) * mm});
            skLineSegment(sketch, "E405", {"start": v(-59.35, 69.91) * mm, "end": v(-58.75, 69.67) * mm});
            skLineSegment(sketch, "E406", {"start": v(-58.75, 69.67) * mm, "end": v(-58.23, 69.27) * mm});
            skLineSegment(sketch, "E407", {"start": v(-58.23, 69.27) * mm, "end": v(-57.83, 68.75) * mm});
            skLineSegment(sketch, "E408", {"start": v(-61.45, 67.89) * mm, "end": v(-61.5, 67.5) * mm});
            skLineSegment(sketch, "E409", {"start": v(-61.5, 67.5) * mm, "end": v(-61.45, 67.11) * mm});
            skLineSegment(sketch, "E410", {"start": v(-61.45, 67.11) * mm, "end": v(-61.3, 66.75) * mm});
            skLineSegment(sketch, "E411", {"start": v(-61.3, 66.75) * mm, "end": v(-61.06, 66.44) * mm});
            skLineSegment(sketch, "E412", {"start": v(-61.06, 66.44) * mm, "end": v(-60.75, 66.2) * mm});
            skLineSegment(sketch, "E413", {"start": v(-60.75, 66.2) * mm, "end": v(-60.39, 66.05) * mm});
            skLineSegment(sketch, "E414", {"start": v(-60.39, 66.05) * mm, "end": v(-60, 66) * mm});
            skLineSegment(sketch, "E415", {"start": v(-60, 66) * mm, "end": v(-59.61, 66.05) * mm});
            skLineSegment(sketch, "E416", {"start": v(-59.61, 66.05) * mm, "end": v(-59.25, 66.2) * mm});
            skLineSegment(sketch, "E417", {"start": v(-59.25, 66.2) * mm, "end": v(-58.94, 66.44) * mm});
            skLineSegment(sketch, "E418", {"start": v(-58.94, 66.44) * mm, "end": v(-58.7, 66.75) * mm});
            skLineSegment(sketch, "E419", {"start": v(-58.7, 66.75) * mm, "end": v(-58.55, 67.11) * mm});
            skLineSegment(sketch, "E420", {"start": v(-58.55, 67.11) * mm, "end": v(-58.5, 67.5) * mm});
            skLineSegment(sketch, "E421", {"start": v(-58.5, 67.5) * mm, "end": v(-58.55, 67.89) * mm});
            skLineSegment(sketch, "E422", {"start": v(-58.55, 67.89) * mm, "end": v(-58.7, 68.25) * mm});
            skLineSegment(sketch, "E423", {"start": v(-58.7, 68.25) * mm, "end": v(-58.94, 68.56) * mm});
            skLineSegment(sketch, "E424", {"start": v(-58.94, 68.56) * mm, "end": v(-59.25, 68.8) * mm});
            skLineSegment(sketch, "E425", {"start": v(-59.25, 68.8) * mm, "end": v(-59.61, 68.95) * mm});
            skLineSegment(sketch, "E426", {"start": v(-59.61, 68.95) * mm, "end": v(-60, 69) * mm});
            skLineSegment(sketch, "E427", {"start": v(-60, 69) * mm, "end": v(-60.39, 68.95) * mm});
            skLineSegment(sketch, "E428", {"start": v(-60.39, 68.95) * mm, "end": v(-60.75, 68.8) * mm});
            skLineSegment(sketch, "E429", {"start": v(-60.75, 68.8) * mm, "end": v(-61.06, 68.56) * mm});
            skLineSegment(sketch, "E430", {"start": v(-61.06, 68.56) * mm, "end": v(-61.3, 68.25) * mm});
            skLineSegment(sketch, "E431", {"start": v(-61.3, 68.25) * mm, "end": v(-61.45, 67.89) * mm});
            skLineSegment(sketch, "E432", {"start": v(100.57, -69.63) * mm, "end": v(100, -69.7) * mm});
            skLineSegment(sketch, "E433", {"start": v(100, -69.7) * mm, "end": v(99.43, -69.63) * mm});
            skLineSegment(sketch, "E434", {"start": v(99.43, -69.63) * mm, "end": v(98.9, -69.4) * mm});
            skLineSegment(sketch, "E435", {"start": v(98.9, -69.4) * mm, "end": v(98.44, -69.06) * mm});
            skLineSegment(sketch, "E436", {"start": v(98.44, -69.06) * mm, "end": v(98.1, -68.6) * mm});
            skLineSegment(sketch, "E437", {"start": v(98.1, -68.6) * mm, "end": v(97.87, -68.07) * mm});
            skLineSegment(sketch, "E438", {"start": v(97.87, -68.07) * mm, "end": v(97.8, -67.5) * mm});
            skLineSegment(sketch, "E439", {"start": v(97.8, -67.5) * mm, "end": v(97.87, -66.93) * mm});
            skLineSegment(sketch, "E440", {"start": v(97.87, -66.93) * mm, "end": v(98.1, -66.4) * mm});
            skLineSegment(sketch, "E441", {"start": v(98.1, -66.4) * mm, "end": v(98.44, -65.94) * mm});
            skLineSegment(sketch, "E442", {"start": v(98.44, -65.94) * mm, "end": v(98.9, -65.6) * mm});
            skLineSegment(sketch, "E443", {"start": v(98.9, -65.6) * mm, "end": v(99.43, -65.37) * mm});
            skLineSegment(sketch, "E444", {"start": v(99.43, -65.37) * mm, "end": v(100, -65.3) * mm});
            skLineSegment(sketch, "E445", {"start": v(100, -65.3) * mm, "end": v(100.57, -65.37) * mm});
            skLineSegment(sketch, "E446", {"start": v(100.57, -65.37) * mm, "end": v(101.1, -65.6) * mm});
            skLineSegment(sketch, "E447", {"start": v(101.1, -65.6) * mm, "end": v(101.56, -65.94) * mm});
            skLineSegment(sketch, "E448", {"start": v(101.56, -65.94) * mm, "end": v(101.9, -66.4) * mm});
            skLineSegment(sketch, "E449", {"start": v(101.9, -66.4) * mm, "end": v(102.13, -66.93) * mm});
            skLineSegment(sketch, "E450", {"start": v(102.13, -66.93) * mm, "end": v(102.2, -67.5) * mm});
            skLineSegment(sketch, "E451", {"start": v(102.2, -67.5) * mm, "end": v(102.13, -68.07) * mm});
            skLineSegment(sketch, "E452", {"start": v(102.13, -68.07) * mm, "end": v(101.9, -68.6) * mm});
            skLineSegment(sketch, "E453", {"start": v(101.9, -68.6) * mm, "end": v(101.56, -69.06) * mm});
            skLineSegment(sketch, "E454", {"start": v(101.56, -69.06) * mm, "end": v(101.1, -69.4) * mm});
            skLineSegment(sketch, "E455", {"start": v(101.1, -69.4) * mm, "end": v(100.57, -69.63) * mm});
            skLineSegment(sketch, "E456", {"start": v(99.61, -66.05) * mm, "end": v(99.25, -66.2) * mm});
            skLineSegment(sketch, "E457", {"start": v(99.25, -66.2) * mm, "end": v(98.94, -66.44) * mm});
            skLineSegment(sketch, "E458", {"start": v(98.94, -66.44) * mm, "end": v(98.7, -66.75) * mm});
            skLineSegment(sketch, "E459", {"start": v(98.7, -66.75) * mm, "end": v(98.55, -67.11) * mm});
            skLineSegment(sketch, "E460", {"start": v(98.55, -67.11) * mm, "end": v(98.5, -67.5) * mm});
            skLineSegment(sketch, "E461", {"start": v(98.5, -67.5) * mm, "end": v(98.55, -67.89) * mm});
            skLineSegment(sketch, "E462", {"start": v(98.55, -67.89) * mm, "end": v(98.7, -68.25) * mm});
            skLineSegment(sketch, "E463", {"start": v(98.7, -68.25) * mm, "end": v(98.94, -68.56) * mm});
            skLineSegment(sketch, "E464", {"start": v(98.94, -68.56) * mm, "end": v(99.25, -68.8) * mm});
            skLineSegment(sketch, "E465", {"start": v(99.25, -68.8) * mm, "end": v(99.61, -68.95) * mm});
            skLineSegment(sketch, "E466", {"start": v(99.61, -68.95) * mm, "end": v(100, -69) * mm});
            skLineSegment(sketch, "E467", {"start": v(100, -69) * mm, "end": v(100.39, -68.95) * mm});
            skLineSegment(sketch, "E468", {"start": v(100.39, -68.95) * mm, "end": v(100.75, -68.8) * mm});
            skLineSegment(sketch, "E469", {"start": v(100.75, -68.8) * mm, "end": v(101.06, -68.56) * mm});
            skLineSegment(sketch, "E470", {"start": v(101.06, -68.56) * mm, "end": v(101.3, -68.25) * mm});
            skLineSegment(sketch, "E471", {"start": v(101.3, -68.25) * mm, "end": v(101.45, -67.89) * mm});
            skLineSegment(sketch, "E472", {"start": v(101.45, -67.89) * mm, "end": v(101.5, -67.5) * mm});
            skLineSegment(sketch, "E473", {"start": v(101.5, -67.5) * mm, "end": v(101.45, -67.11) * mm});
            skLineSegment(sketch, "E474", {"start": v(101.45, -67.11) * mm, "end": v(101.3, -66.75) * mm});
            skLineSegment(sketch, "E475", {"start": v(101.3, -66.75) * mm, "end": v(101.06, -66.44) * mm});
            skLineSegment(sketch, "E476", {"start": v(101.06, -66.44) * mm, "end": v(100.75, -66.2) * mm});
            skLineSegment(sketch, "E477", {"start": v(100.75, -66.2) * mm, "end": v(100.39, -66.05) * mm});
            skLineSegment(sketch, "E478", {"start": v(100.39, -66.05) * mm, "end": v(100, -66) * mm});
            skLineSegment(sketch, "E479", {"start": v(100, -66) * mm, "end": v(99.61, -66.05) * mm});
            skLineSegment(sketch, "E480", {"start": v(-61.25, -65.33) * mm, "end": v(-60.65, -65.09) * mm});
            skLineSegment(sketch, "E481", {"start": v(-60.65, -65.09) * mm, "end": v(-60, -65) * mm});
            skLineSegment(sketch, "E482", {"start": v(-60, -65) * mm, "end": v(-59.35, -65.09) * mm});
            skLineSegment(sketch, "E483", {"start": v(-59.35, -65.09) * mm, "end": v(-58.75, -65.33) * mm});
            skLineSegment(sketch, "E484", {"start": v(-58.75, -65.33) * mm, "end": v(-58.23, -65.73) * mm});
            skLineSegment(sketch, "E485", {"start": v(-58.23, -65.73) * mm, "end": v(-57.83, -66.25) * mm});
            skLineSegment(sketch, "E486", {"start": v(-57.83, -66.25) * mm, "end": v(-57.59, -66.85) * mm});
            skLineSegment(sketch, "E487", {"start": v(-57.59, -66.85) * mm, "end": v(-57.5, -67.5) * mm});
            skLineSegment(sketch, "E488", {"start": v(-57.5, -67.5) * mm, "end": v(-57.59, -68.15) * mm});
            skLineSegment(sketch, "E489", {"start": v(-57.59, -68.15) * mm, "end": v(-57.83, -68.75) * mm});
            skLineSegment(sketch, "E490", {"start": v(-57.83, -68.75) * mm, "end": v(-58.23, -69.27) * mm});
            skLineSegment(sketch, "E491", {"start": v(-58.23, -69.27) * mm, "end": v(-58.75, -69.67) * mm});
            skLineSegment(sketch, "E492", {"start": v(-58.75, -69.67) * mm, "end": v(-59.35, -69.91) * mm});
            skLineSegment(sketch, "E493", {"start": v(-59.35, -69.91) * mm, "end": v(-60, -70) * mm});
            skLineSegment(sketch, "E494", {"start": v(-60, -70) * mm, "end": v(-60.65, -69.91) * mm});
            skLineSegment(sketch, "E495", {"start": v(-60.65, -69.91) * mm, "end": v(-61.25, -69.67) * mm});
            skLineSegment(sketch, "E496", {"start": v(-61.25, -69.67) * mm, "end": v(-61.77, -69.27) * mm});
            skLineSegment(sketch, "E497", {"start": v(-61.77, -69.27) * mm, "end": v(-62.17, -68.75) * mm});
            skLineSegment(sketch, "E498", {"start": v(-62.17, -68.75) * mm, "end": v(-62.41, -68.15) * mm});
            skLineSegment(sketch, "E499", {"start": v(-62.41, -68.15) * mm, "end": v(-62.5, -67.5) * mm});
            skLineSegment(sketch, "E500", {"start": v(-62.5, -67.5) * mm, "end": v(-62.41, -66.85) * mm});
            skLineSegment(sketch, "E501", {"start": v(-62.41, -66.85) * mm, "end": v(-62.17, -66.25) * mm});
            skLineSegment(sketch, "E502", {"start": v(-62.17, -66.25) * mm, "end": v(-61.77, -65.73) * mm});
            skLineSegment(sketch, "E503", {"start": v(-61.77, -65.73) * mm, "end": v(-61.25, -65.33) * mm});
            skLineSegment(sketch, "E504", {"start": v(-58.7, -68.25) * mm, "end": v(-58.55, -67.89) * mm});
            skLineSegment(sketch, "E505", {"start": v(-58.55, -67.89) * mm, "end": v(-58.5, -67.5) * mm});
            skLineSegment(sketch, "E506", {"start": v(-58.5, -67.5) * mm, "end": v(-58.55, -67.11) * mm});
            skLineSegment(sketch, "E507", {"start": v(-58.55, -67.11) * mm, "end": v(-58.7, -66.75) * mm});
            skLineSegment(sketch, "E508", {"start": v(-58.7, -66.75) * mm, "end": v(-58.94, -66.44) * mm});
            skLineSegment(sketch, "E509", {"start": v(-58.94, -66.44) * mm, "end": v(-59.25, -66.2) * mm});
            skLineSegment(sketch, "E510", {"start": v(-59.25, -66.2) * mm, "end": v(-59.61, -66.05) * mm});
            skLineSegment(sketch, "E511", {"start": v(-59.61, -66.05) * mm, "end": v(-60, -66) * mm});
            skLineSegment(sketch, "E512", {"start": v(-60, -66) * mm, "end": v(-60.39, -66.05) * mm});
            skLineSegment(sketch, "E513", {"start": v(-60.39, -66.05) * mm, "end": v(-60.75, -66.2) * mm});
            skLineSegment(sketch, "E514", {"start": v(-60.75, -66.2) * mm, "end": v(-61.06, -66.44) * mm});
            skLineSegment(sketch, "E515", {"start": v(-61.06, -66.44) * mm, "end": v(-61.3, -66.75) * mm});
            skLineSegment(sketch, "E516", {"start": v(-61.3, -66.75) * mm, "end": v(-61.45, -67.11) * mm});
            skLineSegment(sketch, "E517", {"start": v(-61.45, -67.11) * mm, "end": v(-61.5, -67.5) * mm});
            skLineSegment(sketch, "E518", {"start": v(-61.5, -67.5) * mm, "end": v(-61.45, -67.89) * mm});
            skLineSegment(sketch, "E519", {"start": v(-61.45, -67.89) * mm, "end": v(-61.3, -68.25) * mm});
            skLineSegment(sketch, "E520", {"start": v(-61.3, -68.25) * mm, "end": v(-61.06, -68.56) * mm});
            skLineSegment(sketch, "E521", {"start": v(-61.06, -68.56) * mm, "end": v(-60.75, -68.8) * mm});
            skLineSegment(sketch, "E522", {"start": v(-60.75, -68.8) * mm, "end": v(-60.39, -68.95) * mm});
            skLineSegment(sketch, "E523", {"start": v(-60.39, -68.95) * mm, "end": v(-60, -69) * mm});
            skLineSegment(sketch, "E524", {"start": v(-60, -69) * mm, "end": v(-59.61, -68.95) * mm});
            skLineSegment(sketch, "E525", {"start": v(-59.61, -68.95) * mm, "end": v(-59.25, -68.8) * mm});
            skLineSegment(sketch, "E526", {"start": v(-59.25, -68.8) * mm, "end": v(-58.94, -68.56) * mm});
            skLineSegment(sketch, "E527", {"start": v(-58.94, -68.56) * mm, "end": v(-58.7, -68.25) * mm});
            skLineSegment(sketch, "E528", {"start": v(150, 90) * mm, "end": v(150, -90) * mm});
            skLineSegment(sketch, "E529", {"start": v(150, -90) * mm, "end": v(149.91, -91.3) * mm});
            skLineSegment(sketch, "E530", {"start": v(149.91, -91.3) * mm, "end": v(149.66, -92.59) * mm});
            skLineSegment(sketch, "E531", {"start": v(149.66, -92.59) * mm, "end": v(149.24, -93.83) * mm});
            skLineSegment(sketch, "E532", {"start": v(149.24, -93.83) * mm, "end": v(148.66, -95) * mm});
            skLineSegment(sketch, "E533", {"start": v(148.66, -95) * mm, "end": v(147.93, -96.09) * mm});
            skLineSegment(sketch, "E534", {"start": v(147.93, -96.09) * mm, "end": v(147.07, -97.07) * mm});
            skLineSegment(sketch, "E535", {"start": v(147.07, -97.07) * mm, "end": v(146.09, -97.93) * mm});
            skLineSegment(sketch, "E536", {"start": v(146.09, -97.93) * mm, "end": v(145, -98.66) * mm});
            skLineSegment(sketch, "E537", {"start": v(145, -98.66) * mm, "end": v(143.83, -99.24) * mm});
            skLineSegment(sketch, "E538", {"start": v(143.83, -99.24) * mm, "end": v(142.59, -99.66) * mm});
            skLineSegment(sketch, "E539", {"start": v(142.59, -99.66) * mm, "end": v(141.3, -99.91) * mm});
            skLineSegment(sketch, "E540", {"start": v(141.3, -99.91) * mm, "end": v(140, -100) * mm});
            skLineSegment(sketch, "E541", {"start": v(140, -100) * mm, "end": v(-140, -100) * mm});
            skLineSegment(sketch, "E542", {"start": v(-140, -100) * mm, "end": v(-141.3, -99.91) * mm});
            skLineSegment(sketch, "E543", {"start": v(-141.3, -99.91) * mm, "end": v(-142.59, -99.66) * mm});
            skLineSegment(sketch, "E544", {"start": v(-142.59, -99.66) * mm, "end": v(-143.83, -99.24) * mm});
            skLineSegment(sketch, "E545", {"start": v(-143.83, -99.24) * mm, "end": v(-145, -98.66) * mm});
            skLineSegment(sketch, "E546", {"start": v(-145, -98.66) * mm, "end": v(-146.09, -97.93) * mm});
            skLineSegment(sketch, "E547", {"start": v(-146.09, -97.93) * mm, "end": v(-147.07, -97.07) * mm});
            skLineSegment(sketch, "E548", {"start": v(-147.07, -97.07) * mm, "end": v(-147.93, -96.09) * mm});
            skLineSegment(sketch, "E549", {"start": v(-147.93, -96.09) * mm, "end": v(-148.66, -95) * mm});
            skLineSegment(sketch, "E550", {"start": v(-148.66, -95) * mm, "end": v(-149.24, -93.83) * mm});
            skLineSegment(sketch, "E551", {"start": v(-149.24, -93.83) * mm, "end": v(-149.66, -92.59) * mm});
            skLineSegment(sketch, "E552", {"start": v(-149.66, -92.59) * mm, "end": v(-149.91, -91.3) * mm});
            skLineSegment(sketch, "E553", {"start": v(-149.91, -91.3) * mm, "end": v(-150, -90) * mm});
            skLineSegment(sketch, "E554", {"start": v(-150, -90) * mm, "end": v(-150, 90) * mm});
            skLineSegment(sketch, "E555", {"start": v(-150, 90) * mm, "end": v(-149.91, 91.3) * mm});
            skLineSegment(sketch, "E556", {"start": v(-149.91, 91.3) * mm, "end": v(-149.66, 92.59) * mm});
            skLineSegment(sketch, "E557", {"start": v(-149.66, 92.59) * mm, "end": v(-149.24, 93.83) * mm});
            skLineSegment(sketch, "E558", {"start": v(-149.24, 93.83) * mm, "end": v(-148.66, 95) * mm});
            skLineSegment(sketch, "E559", {"start": v(-148.66, 95) * mm, "end": v(-147.93, 96.09) * mm});
            skLineSegment(sketch, "E560", {"start": v(-147.93, 96.09) * mm, "end": v(-147.07, 97.07) * mm});
            skLineSegment(sketch, "E561", {"start": v(-147.07, 97.07) * mm, "end": v(-146.09, 97.93) * mm});
            skLineSegment(sketch, "E562", {"start": v(-146.09, 97.93) * mm, "end": v(-145, 98.66) * mm});
            skLineSegment(sketch, "E563", {"start": v(-145, 98.66) * mm, "end": v(-143.83, 99.24) * mm});
            skLineSegment(sketch, "E564", {"start": v(-143.83, 99.24) * mm, "end": v(-142.59, 99.66) * mm});
            skLineSegment(sketch, "E565", {"start": v(-142.59, 99.66) * mm, "end": v(-141.3, 99.91) * mm});
            skLineSegment(sketch, "E566", {"start": v(-141.3, 99.91) * mm, "end": v(-140, 100) * mm});
            skLineSegment(sketch, "E567", {"start": v(-140, 100) * mm, "end": v(140, 100) * mm});
            skLineSegment(sketch, "E568", {"start": v(140, 100) * mm, "end": v(141.3, 99.91) * mm});
            skLineSegment(sketch, "E569", {"start": v(141.3, 99.91) * mm, "end": v(142.59, 99.66) * mm});
            skLineSegment(sketch, "E570", {"start": v(142.59, 99.66) * mm, "end": v(143.83, 99.24) * mm});
            skLineSegment(sketch, "E571", {"start": v(143.83, 99.24) * mm, "end": v(145, 98.66) * mm});
            skLineSegment(sketch, "E572", {"start": v(145, 98.66) * mm, "end": v(146.09, 97.93) * mm});
            skLineSegment(sketch, "E573", {"start": v(146.09, 97.93) * mm, "end": v(147.07, 97.07) * mm});
            skLineSegment(sketch, "E574", {"start": v(147.07, 97.07) * mm, "end": v(147.93, 96.09) * mm});
            skLineSegment(sketch, "E575", {"start": v(147.93, 96.09) * mm, "end": v(148.66, 95) * mm});
            skLineSegment(sketch, "E576", {"start": v(148.66, 95) * mm, "end": v(149.24, 93.83) * mm});
            skLineSegment(sketch, "E577", {"start": v(149.24, 93.83) * mm, "end": v(149.66, 92.59) * mm});
            skLineSegment(sketch, "E578", {"start": v(149.66, 92.59) * mm, "end": v(149.91, 91.3) * mm});
            skLineSegment(sketch, "E579", {"start": v(149.91, 91.3) * mm, "end": v(150, 90) * mm});
            skLineSegment(sketch, "E580", {"start": v(-132.17, 81.25) * mm, "end": v(-132.41, 80.65) * mm});
            skLineSegment(sketch, "E581", {"start": v(-132.41, 80.65) * mm, "end": v(-132.41, 20.65) * mm});
            skLineSegment(sketch, "E582", {"start": v(-132.41, 20.65) * mm, "end": v(-132.5, 20) * mm});
            skLineSegment(sketch, "E583", {"start": v(-132.5, 20) * mm, "end": v(-132.41, 19.35) * mm});
            skLineSegment(sketch, "E584", {"start": v(-132.41, 19.35) * mm, "end": v(-132.17, 18.75) * mm});
            skLineSegment(sketch, "E585", {"start": v(-132.17, 18.75) * mm, "end": v(-131.77, 18.23) * mm});
            skLineSegment(sketch, "E586", {"start": v(-131.77, 18.23) * mm, "end": v(-131.25, 17.83) * mm});
            skLineSegment(sketch, "E587", {"start": v(-131.25, 17.83) * mm, "end": v(-130.65, 17.59) * mm});
            skLineSegment(sketch, "E588", {"start": v(-130.65, 17.59) * mm, "end": v(-130, 17.5) * mm});
            skLineSegment(sketch, "E589", {"start": v(-130, 17.5) * mm, "end": v(-129.35, 17.59) * mm});
            skLineSegment(sketch, "E590", {"start": v(-129.35, 17.59) * mm, "end": v(-128.75, 17.83) * mm});
            skLineSegment(sketch, "E591", {"start": v(-128.75, 17.83) * mm, "end": v(-128.23, 18.23) * mm});
            skLineSegment(sketch, "E592", {"start": v(-128.23, 18.23) * mm, "end": v(-127.83, 18.75) * mm});
            skLineSegment(sketch, "E593", {"start": v(-127.83, 18.75) * mm, "end": v(-127.59, 19.35) * mm});
            skLineSegment(sketch, "E594", {"start": v(-127.59, 19.35) * mm, "end": v(-127.5, 20) * mm});
            skLineSegment(sketch, "E595", {"start": v(-127.5, 20) * mm, "end": v(-127.5, 80) * mm});
            skLineSegment(sketch, "E596", {"start": v(-127.5, 80) * mm, "end": v(-127.59, 80.65) * mm});
            skLineSegment(sketch, "E597", {"start": v(-127.59, 80.65) * mm, "end": v(-127.83, 81.25) * mm});
            skLineSegment(sketch, "E598", {"start": v(-127.83, 81.25) * mm, "end": v(-128.23, 81.77) * mm});
            skLineSegment(sketch, "E599", {"start": v(-128.23, 81.77) * mm, "end": v(-128.75, 82.17) * mm});
            skLineSegment(sketch, "E600", {"start": v(-128.75, 82.17) * mm, "end": v(-129.35, 82.41) * mm});
            skLineSegment(sketch, "E601", {"start": v(-129.35, 82.41) * mm, "end": v(-130, 82.5) * mm});
            skLineSegment(sketch, "E602", {"start": v(-130, 82.5) * mm, "end": v(-130.65, 82.41) * mm});
            skLineSegment(sketch, "E603", {"start": v(-130.65, 82.41) * mm, "end": v(-131.25, 82.17) * mm});
            skLineSegment(sketch, "E604", {"start": v(-131.25, 82.17) * mm, "end": v(-131.77, 81.77) * mm});
            skLineSegment(sketch, "E605", {"start": v(-131.77, 81.77) * mm, "end": v(-132.17, 81.25) * mm});
            skLineSegment(sketch, "E606", {"start": v(-132.41, -19.35) * mm, "end": v(-132.5, -20) * mm});
            skLineSegment(sketch, "E607", {"start": v(-132.5, -20) * mm, "end": v(-132.5, -80) * mm});
            skLineSegment(sketch, "E608", {"start": v(-132.5, -80) * mm, "end": v(-132.41, -80.65) * mm});
            skLineSegment(sketch, "E609", {"start": v(-132.41, -80.65) * mm, "end": v(-132.17, -81.25) * mm});
            skLineSegment(sketch, "E610", {"start": v(-132.17, -81.25) * mm, "end": v(-131.77, -81.77) * mm});
            skLineSegment(sketch, "E611", {"start": v(-131.77, -81.77) * mm, "end": v(-131.25, -82.17) * mm});
            skLineSegment(sketch, "E612", {"start": v(-131.25, -82.17) * mm, "end": v(-130.65, -82.41) * mm});
            skLineSegment(sketch, "E613", {"start": v(-130.65, -82.41) * mm, "end": v(-130, -82.5) * mm});
            skLineSegment(sketch, "E614", {"start": v(-130, -82.5) * mm, "end": v(-129.35, -82.41) * mm});
            skLineSegment(sketch, "E615", {"start": v(-129.35, -82.41) * mm, "end": v(-128.75, -82.17) * mm});
            skLineSegment(sketch, "E616", {"start": v(-128.75, -82.17) * mm, "end": v(-128.23, -81.77) * mm});
            skLineSegment(sketch, "E617", {"start": v(-128.23, -81.77) * mm, "end": v(-127.83, -81.25) * mm});
            skLineSegment(sketch, "E618", {"start": v(-127.83, -81.25) * mm, "end": v(-127.59, -80.65) * mm});
            skLineSegment(sketch, "E619", {"start": v(-127.59, -80.65) * mm, "end": v(-127.5, -80) * mm});
            skLineSegment(sketch, "E620", {"start": v(-127.5, -80) * mm, "end": v(-127.5, -20) * mm});
            skLineSegment(sketch, "E621", {"start": v(-127.5, -20) * mm, "end": v(-127.59, -19.35) * mm});
            skLineSegment(sketch, "E622", {"start": v(-127.59, -19.35) * mm, "end": v(-127.83, -18.75) * mm});
            skLineSegment(sketch, "E623", {"start": v(-127.83, -18.75) * mm, "end": v(-128.23, -18.23) * mm});
            skLineSegment(sketch, "E624", {"start": v(-128.23, -18.23) * mm, "end": v(-128.75, -17.83) * mm});
            skLineSegment(sketch, "E625", {"start": v(-128.75, -17.83) * mm, "end": v(-129.35, -17.59) * mm});
            skLineSegment(sketch, "E626", {"start": v(-129.35, -17.59) * mm, "end": v(-130, -17.5) * mm});
            skLineSegment(sketch, "E627", {"start": v(-130, -17.5) * mm, "end": v(-130.65, -17.59) * mm});
            skLineSegment(sketch, "E628", {"start": v(-130.65, -17.59) * mm, "end": v(-131.25, -17.83) * mm});
            skLineSegment(sketch, "E629", {"start": v(-131.25, -17.83) * mm, "end": v(-131.77, -18.23) * mm});
            skLineSegment(sketch, "E630", {"start": v(-131.77, -18.23) * mm, "end": v(-132.17, -18.75) * mm});
            skLineSegment(sketch, "E631", {"start": v(-132.17, -18.75) * mm, "end": v(-132.41, -19.35) * mm});
            skLineSegment(sketch, "E632", {"start": v(127.59, 80.65) * mm, "end": v(127.5, 80) * mm});
            skLineSegment(sketch, "E633", {"start": v(127.5, 80) * mm, "end": v(127.5, 20) * mm});
            skLineSegment(sketch, "E634", {"start": v(127.5, 20) * mm, "end": v(127.59, 19.35) * mm});
            skLineSegment(sketch, "E635", {"start": v(127.59, 19.35) * mm, "end": v(127.83, 18.75) * mm});
            skLineSegment(sketch, "E636", {"start": v(127.83, 18.75) * mm, "end": v(128.23, 18.23) * mm});
            skLineSegment(sketch, "E637", {"start": v(128.23, 18.23) * mm, "end": v(128.75, 17.83) * mm});
            skLineSegment(sketch, "E638", {"start": v(128.75, 17.83) * mm, "end": v(129.35, 17.59) * mm});
            skLineSegment(sketch, "E639", {"start": v(129.35, 17.59) * mm, "end": v(130, 17.5) * mm});
            skLineSegment(sketch, "E640", {"start": v(130, 17.5) * mm, "end": v(130.65, 17.59) * mm});
            skLineSegment(sketch, "E641", {"start": v(130.65, 17.59) * mm, "end": v(131.25, 17.83) * mm});
            skLineSegment(sketch, "E642", {"start": v(131.25, 17.83) * mm, "end": v(131.77, 18.23) * mm});
            skLineSegment(sketch, "E643", {"start": v(131.77, 18.23) * mm, "end": v(132.17, 18.75) * mm});
            skLineSegment(sketch, "E644", {"start": v(132.17, 18.75) * mm, "end": v(132.41, 19.35) * mm});
            skLineSegment(sketch, "E645", {"start": v(132.41, 19.35) * mm, "end": v(132.5, 20) * mm});
            skLineSegment(sketch, "E646", {"start": v(132.5, 20) * mm, "end": v(132.5, 80) * mm});
            skLineSegment(sketch, "E647", {"start": v(132.5, 80) * mm, "end": v(132.41, 80.65) * mm});
            skLineSegment(sketch, "E648", {"start": v(132.41, 80.65) * mm, "end": v(132.17, 81.25) * mm});
            skLineSegment(sketch, "E649", {"start": v(132.17, 81.25) * mm, "end": v(131.77, 81.77) * mm});
            skLineSegment(sketch, "E650", {"start": v(131.77, 81.77) * mm, "end": v(131.25, 82.17) * mm});
            skLineSegment(sketch, "E651", {"start": v(131.25, 82.17) * mm, "end": v(130.65, 82.41) * mm});
            skLineSegment(sketch, "E652", {"start": v(130.65, 82.41) * mm, "end": v(130, 82.5) * mm});
            skLineSegment(sketch, "E653", {"start": v(130, 82.5) * mm, "end": v(129.35, 82.41) * mm});
            skLineSegment(sketch, "E654", {"start": v(129.35, 82.41) * mm, "end": v(128.75, 82.17) * mm});
            skLineSegment(sketch, "E655", {"start": v(128.75, 82.17) * mm, "end": v(128.23, 81.77) * mm});
            skLineSegment(sketch, "E656", {"start": v(128.23, 81.77) * mm, "end": v(127.83, 81.25) * mm});
            skLineSegment(sketch, "E657", {"start": v(127.83, 81.25) * mm, "end": v(127.59, 80.65) * mm});
            skLineSegment(sketch, "E658", {"start": v(132.41, -80.65) * mm, "end": v(132.5, -80) * mm});
            skLineSegment(sketch, "E659", {"start": v(132.5, -80) * mm, "end": v(132.5, -20) * mm});
            skLineSegment(sketch, "E660", {"start": v(132.5, -20) * mm, "end": v(132.41, -19.35) * mm});
            skLineSegment(sketch, "E661", {"start": v(132.41, -19.35) * mm, "end": v(132.17, -18.75) * mm});
            skLineSegment(sketch, "E662", {"start": v(132.17, -18.75) * mm, "end": v(131.77, -18.23) * mm});
            skLineSegment(sketch, "E663", {"start": v(131.77, -18.23) * mm, "end": v(131.25, -17.83) * mm});
            skLineSegment(sketch, "E664", {"start": v(131.25, -17.83) * mm, "end": v(130.65, -17.59) * mm});
            skLineSegment(sketch, "E665", {"start": v(130.65, -17.59) * mm, "end": v(130, -17.5) * mm});
            skLineSegment(sketch, "E666", {"start": v(130, -17.5) * mm, "end": v(129.35, -17.59) * mm});
            skLineSegment(sketch, "E667", {"start": v(129.35, -17.59) * mm, "end": v(128.75, -17.83) * mm});
            skLineSegment(sketch, "E668", {"start": v(128.75, -17.83) * mm, "end": v(128.23, -18.23) * mm});
            skLineSegment(sketch, "E669", {"start": v(128.23, -18.23) * mm, "end": v(127.83, -18.75) * mm});
            skLineSegment(sketch, "E670", {"start": v(127.83, -18.75) * mm, "end": v(127.59, -19.35) * mm});
            skLineSegment(sketch, "E671", {"start": v(127.59, -19.35) * mm, "end": v(127.5, -20) * mm});
            skLineSegment(sketch, "E672", {"start": v(127.5, -20) * mm, "end": v(127.5, -80) * mm});
            skLineSegment(sketch, "E673", {"start": v(127.5, -80) * mm, "end": v(127.59, -80.65) * mm});
            skLineSegment(sketch, "E674", {"start": v(127.59, -80.65) * mm, "end": v(127.83, -81.25) * mm});
            skLineSegment(sketch, "E675", {"start": v(127.83, -81.25) * mm, "end": v(128.23, -81.77) * mm});
            skLineSegment(sketch, "E676", {"start": v(128.23, -81.77) * mm, "end": v(128.75, -82.17) * mm});
            skLineSegment(sketch, "E677", {"start": v(128.75, -82.17) * mm, "end": v(129.35, -82.41) * mm});
            skLineSegment(sketch, "E678", {"start": v(129.35, -82.41) * mm, "end": v(130, -82.5) * mm});
            skLineSegment(sketch, "E679", {"start": v(130, -82.5) * mm, "end": v(130.65, -82.41) * mm});
            skLineSegment(sketch, "E680", {"start": v(130.65, -82.41) * mm, "end": v(131.25, -82.17) * mm});
            skLineSegment(sketch, "E681", {"start": v(131.25, -82.17) * mm, "end": v(131.77, -81.77) * mm});
            skLineSegment(sketch, "E682", {"start": v(131.77, -81.77) * mm, "end": v(132.17, -81.25) * mm});
            skLineSegment(sketch, "E683", {"start": v(132.17, -81.25) * mm, "end": v(132.41, -80.65) * mm});
            skLineSegment(sketch, "E684", {"start": v(52.41, -50) * mm, "end": v(52.41, 49.35) * mm});
            skLineSegment(sketch, "E685", {"start": v(52.41, 49.35) * mm, "end": v(52.5, 50) * mm});
            skLineSegment(sketch, "E686", {"start": v(52.5, 50) * mm, "end": v(52.41, 50.65) * mm});
            skLineSegment(sketch, "E687", {"start": v(52.41, 50.65) * mm, "end": v(52.17, 51.25) * mm});
            skLineSegment(sketch, "E688", {"start": v(52.17, 51.25) * mm, "end": v(51.77, 51.77) * mm});
            skLineSegment(sketch, "E689", {"start": v(51.77, 51.77) * mm, "end": v(51.25, 52.17) * mm});
            skLineSegment(sketch, "E690", {"start": v(51.25, 52.17) * mm, "end": v(50.65, 52.41) * mm});
            skLineSegment(sketch, "E691", {"start": v(50.65, 52.41) * mm, "end": v(50, 52.5) * mm});
            skLineSegment(sketch, "E692", {"start": v(50, 52.5) * mm, "end": v(49.35, 52.41) * mm});
            skLineSegment(sketch, "E693", {"start": v(49.35, 52.41) * mm, "end": v(48.75, 52.17) * mm});
            skLineSegment(sketch, "E694", {"start": v(48.75, 52.17) * mm, "end": v(48.23, 51.77) * mm});
            skLineSegment(sketch, "E695", {"start": v(48.23, 51.77) * mm, "end": v(47.83, 51.25) * mm});
            skLineSegment(sketch, "E696", {"start": v(47.83, 51.25) * mm, "end": v(47.59, 50.65) * mm});
            skLineSegment(sketch, "E697", {"start": v(47.59, 50.65) * mm, "end": v(47.5, 50) * mm});
            skLineSegment(sketch, "E698", {"start": v(47.5, 50) * mm, "end": v(47.59, 49.35) * mm});
            skLineSegment(sketch, "E699", {"start": v(47.59, 49.35) * mm, "end": v(47.59, -49.35) * mm});
            skLineSegment(sketch, "E700", {"start": v(47.59, -49.35) * mm, "end": v(47.5, -50) * mm});
            skLineSegment(sketch, "E701", {"start": v(47.5, -50) * mm, "end": v(47.59, -50.65) * mm});
            skLineSegment(sketch, "E702", {"start": v(47.59, -50.65) * mm, "end": v(47.83, -51.25) * mm});
            skLineSegment(sketch, "E703", {"start": v(47.83, -51.25) * mm, "end": v(48.23, -51.77) * mm});
            skLineSegment(sketch, "E704", {"start": v(48.23, -51.77) * mm, "end": v(48.75, -52.17) * mm});
            skLineSegment(sketch, "E705", {"start": v(48.75, -52.17) * mm, "end": v(49.35, -52.41) * mm});
            skLineSegment(sketch, "E706", {"start": v(49.35, -52.41) * mm, "end": v(50, -52.5) * mm});
            skLineSegment(sketch, "E707", {"start": v(50, -52.5) * mm, "end": v(50.65, -52.41) * mm});
            skLineSegment(sketch, "E708", {"start": v(50.65, -52.41) * mm, "end": v(51.25, -52.17) * mm});
            skLineSegment(sketch, "E709", {"start": v(51.25, -52.17) * mm, "end": v(51.77, -51.77) * mm});
            skLineSegment(sketch, "E710", {"start": v(51.77, -51.77) * mm, "end": v(52.17, -51.25) * mm});
            skLineSegment(sketch, "E711", {"start": v(52.17, -51.25) * mm, "end": v(52.41, -50.65) * mm});
            skLineSegment(sketch, "E712", {"start": v(52.41, -50.65) * mm, "end": v(52.5, -50) * mm});
            skLineSegment(sketch, "E713", {"start": v(52.5, -50) * mm, "end": v(52.41, -50) * mm});
            skLineSegment(sketch, "E714", {"start": v(-52.41, 50.65) * mm, "end": v(-52.5, 50) * mm});
            skLineSegment(sketch, "E715", {"start": v(-52.5, 50) * mm, "end": v(-52.5, -50) * mm});
            skLineSegment(sketch, "E716", {"start": v(-52.5, -50) * mm, "end": v(-52.41, -50.65) * mm});
            skLineSegment(sketch, "E717", {"start": v(-52.41, -50.65) * mm, "end": v(-52.17, -51.25) * mm});
            skLineSegment(sketch, "E718", {"start": v(-52.17, -51.25) * mm, "end": v(-51.77, -51.77) * mm});
            skLineSegment(sketch, "E719", {"start": v(-51.77, -51.77) * mm, "end": v(-51.25, -52.17) * mm});
            skLineSegment(sketch, "E720", {"start": v(-51.25, -52.17) * mm, "end": v(-50.65, -52.41) * mm});
            skLineSegment(sketch, "E721", {"start": v(-50.65, -52.41) * mm, "end": v(-50, -52.5) * mm});
            skLineSegment(sketch, "E722", {"start": v(-50, -52.5) * mm, "end": v(-49.35, -52.41) * mm});
            skLineSegment(sketch, "E723", {"start": v(-49.35, -52.41) * mm, "end": v(-48.75, -52.17) * mm});
            skLineSegment(sketch, "E724", {"start": v(-48.75, -52.17) * mm, "end": v(-48.23, -51.77) * mm});
            skLineSegment(sketch, "E725", {"start": v(-48.23, -51.77) * mm, "end": v(-47.83, -51.25) * mm});
            skLineSegment(sketch, "E726", {"start": v(-47.83, -51.25) * mm, "end": v(-47.59, -50.65) * mm});
            skLineSegment(sketch, "E727", {"start": v(-47.59, -50.65) * mm, "end": v(-47.5, -50) * mm});
            skLineSegment(sketch, "E728", {"start": v(-47.5, -50) * mm, "end": v(-47.5, 50) * mm});
            skLineSegment(sketch, "E729", {"start": v(-47.5, 50) * mm, "end": v(-47.59, 50.65) * mm});
            skLineSegment(sketch, "E730", {"start": v(-47.59, 50.65) * mm, "end": v(-47.83, 51.25) * mm});
            skLineSegment(sketch, "E731", {"start": v(-47.83, 51.25) * mm, "end": v(-48.23, 51.77) * mm});
            skLineSegment(sketch, "E732", {"start": v(-48.23, 51.77) * mm, "end": v(-48.75, 52.17) * mm});
            skLineSegment(sketch, "E733", {"start": v(-48.75, 52.17) * mm, "end": v(-49.35, 52.41) * mm});
            skLineSegment(sketch, "E734", {"start": v(-49.35, 52.41) * mm, "end": v(-50, 52.5) * mm});
            skLineSegment(sketch, "E735", {"start": v(-50, 52.5) * mm, "end": v(-50.65, 52.41) * mm});
            skLineSegment(sketch, "E736", {"start": v(-50.65, 52.41) * mm, "end": v(-51.25, 52.17) * mm});
            skLineSegment(sketch, "E737", {"start": v(-51.25, 52.17) * mm, "end": v(-51.77, 51.77) * mm});
            skLineSegment(sketch, "E738", {"start": v(-51.77, 51.77) * mm, "end": v(-52.17, 51.25) * mm});
            skLineSegment(sketch, "E739", {"start": v(-52.17, 51.25) * mm, "end": v(-52.41, 50.65) * mm});
            skLineSegment(sketch, "E740", {"start": v(100, -69.7) * mm, "end": v(100.57, -69.63) * mm});
            skLineSegment(sketch, "E741", {"start": v(100.57, -69.63) * mm, "end": v(101.1, -69.4) * mm});
            skLineSegment(sketch, "E742", {"start": v(101.1, -69.4) * mm, "end": v(101.56, -69.06) * mm});
            skLineSegment(sketch, "E743", {"start": v(101.56, -69.06) * mm, "end": v(101.9, -68.6) * mm});
            skLineSegment(sketch, "E744", {"start": v(101.9, -68.6) * mm, "end": v(102.13, -68.07) * mm});
            skLineSegment(sketch, "E745", {"start": v(102.13, -68.07) * mm, "end": v(102.2, -67.5) * mm});
            skLineSegment(sketch, "E746", {"start": v(102.2, -67.5) * mm, "end": v(102.13, -66.93) * mm});
            skLineSegment(sketch, "E747", {"start": v(102.13, -66.93) * mm, "end": v(101.9, -66.4) * mm});
            skLineSegment(sketch, "E748", {"start": v(101.9, -66.4) * mm, "end": v(101.56, -65.94) * mm});
            skLineSegment(sketch, "E749", {"start": v(101.56, -65.94) * mm, "end": v(101.1, -65.6) * mm});
            skLineSegment(sketch, "E750", {"start": v(101.1, -65.6) * mm, "end": v(100.57, -65.37) * mm});
            skLineSegment(sketch, "E751", {"start": v(100.57, -65.37) * mm, "end": v(100, -65.3) * mm});
            skLineSegment(sketch, "E752", {"start": v(100, -65.3) * mm, "end": v(99.43, -65.37) * mm});
            skLineSegment(sketch, "E753", {"start": v(99.43, -65.37) * mm, "end": v(98.9, -65.6) * mm});
            skLineSegment(sketch, "E754", {"start": v(98.9, -65.6) * mm, "end": v(98.44, -65.94) * mm});
            skLineSegment(sketch, "E755", {"start": v(98.44, -65.94) * mm, "end": v(98.1, -66.4) * mm});
            skLineSegment(sketch, "E756", {"start": v(98.1, -66.4) * mm, "end": v(97.87, -66.93) * mm});
            skLineSegment(sketch, "E757", {"start": v(97.87, -66.93) * mm, "end": v(97.8, -67.5) * mm});
            skLineSegment(sketch, "E758", {"start": v(97.8, -67.5) * mm, "end": v(97.87, -68.07) * mm});
            skLineSegment(sketch, "E759", {"start": v(97.87, -68.07) * mm, "end": v(98.1, -68.6) * mm});
            skLineSegment(sketch, "E760", {"start": v(98.1, -68.6) * mm, "end": v(98.44, -69.06) * mm});
            skLineSegment(sketch, "E761", {"start": v(98.44, -69.06) * mm, "end": v(98.9, -69.4) * mm});
            skLineSegment(sketch, "E762", {"start": v(98.9, -69.4) * mm, "end": v(99.43, -69.63) * mm});
            skLineSegment(sketch, "E763", {"start": v(99.43, -69.63) * mm, "end": v(100, -69.7) * mm});
            skLineSegment(sketch, "E764", {"start": v(60.57, -65.37) * mm, "end": v(60, -65.3) * mm});
            skLineSegment(sketch, "E765", {"start": v(60, -65.3) * mm, "end": v(59.43, -65.37) * mm});
            skLineSegment(sketch, "E766", {"start": v(59.43, -65.37) * mm, "end": v(58.9, -65.6) * mm});
            skLineSegment(sketch, "E767", {"start": v(58.9, -65.6) * mm, "end": v(58.44, -65.94) * mm});
            skLineSegment(sketch, "E768", {"start": v(58.44, -65.94) * mm, "end": v(58.1, -66.4) * mm});
            skLineSegment(sketch, "E769", {"start": v(58.1, -66.4) * mm, "end": v(57.87, -66.93) * mm});
            skLineSegment(sketch, "E770", {"start": v(57.87, -66.93) * mm, "end": v(57.8, -67.5) * mm});
            skLineSegment(sketch, "E771", {"start": v(57.8, -67.5) * mm, "end": v(57.87, -68.07) * mm});
            skLineSegment(sketch, "E772", {"start": v(57.87, -68.07) * mm, "end": v(58.1, -68.6) * mm});
            skLineSegment(sketch, "E773", {"start": v(58.1, -68.6) * mm, "end": v(58.44, -69.06) * mm});
            skLineSegment(sketch, "E774", {"start": v(58.44, -69.06) * mm, "end": v(58.9, -69.4) * mm});
            skLineSegment(sketch, "E775", {"start": v(58.9, -69.4) * mm, "end": v(59.43, -69.63) * mm});
            skLineSegment(sketch, "E776", {"start": v(59.43, -69.63) * mm, "end": v(60, -69.7) * mm});
            skLineSegment(sketch, "E777", {"start": v(60, -69.7) * mm, "end": v(60.57, -69.63) * mm});
            skLineSegment(sketch, "E778", {"start": v(60.57, -69.63) * mm, "end": v(61.1, -69.4) * mm});
            skLineSegment(sketch, "E779", {"start": v(61.1, -69.4) * mm, "end": v(61.56, -69.06) * mm});
            skLineSegment(sketch, "E780", {"start": v(61.56, -69.06) * mm, "end": v(61.9, -68.6) * mm});
            skLineSegment(sketch, "E781", {"start": v(61.9, -68.6) * mm, "end": v(62.13, -68.07) * mm});
            skLineSegment(sketch, "E782", {"start": v(62.13, -68.07) * mm, "end": v(62.2, -67.5) * mm});
            skLineSegment(sketch, "E783", {"start": v(62.2, -67.5) * mm, "end": v(62.13, -66.93) * mm});
            skLineSegment(sketch, "E784", {"start": v(62.13, -66.93) * mm, "end": v(61.9, -66.4) * mm});
            skLineSegment(sketch, "E785", {"start": v(61.9, -66.4) * mm, "end": v(61.56, -65.94) * mm});
            skLineSegment(sketch, "E786", {"start": v(61.56, -65.94) * mm, "end": v(61.1, -65.6) * mm});
            skLineSegment(sketch, "E787", {"start": v(61.1, -65.6) * mm, "end": v(60.57, -65.37) * mm});
            skLineSegment(sketch, "E788", {"start": v(99.35, 69.91) * mm, "end": v(98.75, 69.67) * mm});
            skLineSegment(sketch, "E789", {"start": v(98.75, 69.67) * mm, "end": v(98.23, 69.27) * mm});
            skLineSegment(sketch, "E790", {"start": v(98.23, 69.27) * mm, "end": v(97.83, 68.75) * mm});
            skLineSegment(sketch, "E791", {"start": v(97.83, 68.75) * mm, "end": v(97.59, 68.15) * mm});
            skLineSegment(sketch, "E792", {"start": v(97.59, 68.15) * mm, "end": v(97.5, 67.5) * mm});
            skLineSegment(sketch, "E793", {"start": v(97.5, 67.5) * mm, "end": v(97.59, 66.85) * mm});
            skLineSegment(sketch, "E794", {"start": v(97.59, 66.85) * mm, "end": v(97.83, 66.25) * mm});
            skLineSegment(sketch, "E795", {"start": v(97.83, 66.25) * mm, "end": v(98.23, 65.73) * mm});
            skLineSegment(sketch, "E796", {"start": v(98.23, 65.73) * mm, "end": v(98.75, 65.33) * mm});
            skLineSegment(sketch, "E797", {"start": v(98.75, 65.33) * mm, "end": v(99.35, 65.09) * mm});
            skLineSegment(sketch, "E798", {"start": v(99.35, 65.09) * mm, "end": v(100, 65) * mm});
            skLineSegment(sketch, "E799", {"start": v(100, 65) * mm, "end": v(100.65, 65.09) * mm});
            skLineSegment(sketch, "E800", {"start": v(100.65, 65.09) * mm, "end": v(101.25, 65.33) * mm});
            skLineSegment(sketch, "E801", {"start": v(101.25, 65.33) * mm, "end": v(101.77, 65.73) * mm});
            skLineSegment(sketch, "E802", {"start": v(101.77, 65.73) * mm, "end": v(102.17, 66.25) * mm});
            skLineSegment(sketch, "E803", {"start": v(102.17, 66.25) * mm, "end": v(102.41, 66.85) * mm});
            skLineSegment(sketch, "E804", {"start": v(102.41, 66.85) * mm, "end": v(102.5, 67.5) * mm});
            skLineSegment(sketch, "E805", {"start": v(102.5, 67.5) * mm, "end": v(102.41, 68.15) * mm});
            skLineSegment(sketch, "E806", {"start": v(102.41, 68.15) * mm, "end": v(102.17, 68.75) * mm});
            skLineSegment(sketch, "E807", {"start": v(102.17, 68.75) * mm, "end": v(101.77, 69.27) * mm});
            skLineSegment(sketch, "E808", {"start": v(101.77, 69.27) * mm, "end": v(101.25, 69.67) * mm});
            skLineSegment(sketch, "E809", {"start": v(101.25, 69.67) * mm, "end": v(100.65, 69.91) * mm});
            skLineSegment(sketch, "E810", {"start": v(100.65, 69.91) * mm, "end": v(100, 70) * mm});
            skLineSegment(sketch, "E811", {"start": v(100, 70) * mm, "end": v(99.35, 69.91) * mm});
            skLineSegment(sketch, "E812", {"start": v(59.35, 65.09) * mm, "end": v(60, 65) * mm});
            skLineSegment(sketch, "E813", {"start": v(60, 65) * mm, "end": v(60.65, 65.09) * mm});
            skLineSegment(sketch, "E814", {"start": v(60.65, 65.09) * mm, "end": v(61.25, 65.33) * mm});
            skLineSegment(sketch, "E815", {"start": v(61.25, 65.33) * mm, "end": v(61.77, 65.73) * mm});
            skLineSegment(sketch, "E816", {"start": v(61.77, 65.73) * mm, "end": v(62.17, 66.25) * mm});
            skLineSegment(sketch, "E817", {"start": v(62.17, 66.25) * mm, "end": v(62.41, 66.85) * mm});
            skLineSegment(sketch, "E818", {"start": v(62.41, 66.85) * mm, "end": v(62.5, 67.5) * mm});
            skLineSegment(sketch, "E819", {"start": v(62.5, 67.5) * mm, "end": v(62.41, 68.15) * mm});
            skLineSegment(sketch, "E820", {"start": v(62.41, 68.15) * mm, "end": v(62.17, 68.75) * mm});
            skLineSegment(sketch, "E821", {"start": v(62.17, 68.75) * mm, "end": v(61.77, 69.27) * mm});
            skLineSegment(sketch, "E822", {"start": v(61.77, 69.27) * mm, "end": v(61.25, 69.67) * mm});
            skLineSegment(sketch, "E823", {"start": v(61.25, 69.67) * mm, "end": v(60.65, 69.91) * mm});
            skLineSegment(sketch, "E824", {"start": v(60.65, 69.91) * mm, "end": v(60, 70) * mm});
            skLineSegment(sketch, "E825", {"start": v(60, 70) * mm, "end": v(59.35, 69.91) * mm});
            skLineSegment(sketch, "E826", {"start": v(59.35, 69.91) * mm, "end": v(58.75, 69.67) * mm});
            skLineSegment(sketch, "E827", {"start": v(58.75, 69.67) * mm, "end": v(58.23, 69.27) * mm});
            skLineSegment(sketch, "E828", {"start": v(58.23, 69.27) * mm, "end": v(57.83, 68.75) * mm});
            skLineSegment(sketch, "E829", {"start": v(57.83, 68.75) * mm, "end": v(57.59, 68.15) * mm});
            skLineSegment(sketch, "E830", {"start": v(57.59, 68.15) * mm, "end": v(57.5, 67.5) * mm});
            skLineSegment(sketch, "E831", {"start": v(57.5, 67.5) * mm, "end": v(57.59, 66.85) * mm});
            skLineSegment(sketch, "E832", {"start": v(57.59, 66.85) * mm, "end": v(57.83, 66.25) * mm});
            skLineSegment(sketch, "E833", {"start": v(57.83, 66.25) * mm, "end": v(58.23, 65.73) * mm});
            skLineSegment(sketch, "E834", {"start": v(58.23, 65.73) * mm, "end": v(58.75, 65.33) * mm});
            skLineSegment(sketch, "E835", {"start": v(58.75, 65.33) * mm, "end": v(59.35, 65.09) * mm});
            skLineSegment(sketch, "E836", {"start": v(20.65, 65.09) * mm, "end": v(21.25, 65.33) * mm});
            skLineSegment(sketch, "E837", {"start": v(21.25, 65.33) * mm, "end": v(21.77, 65.73) * mm});
            skLineSegment(sketch, "E838", {"start": v(21.77, 65.73) * mm, "end": v(22.17, 66.25) * mm});
            skLineSegment(sketch, "E839", {"start": v(22.17, 66.25) * mm, "end": v(22.41, 66.85) * mm});
            skLineSegment(sketch, "E840", {"start": v(22.41, 66.85) * mm, "end": v(22.5, 67.5) * mm});
            skLineSegment(sketch, "E841", {"start": v(22.5, 67.5) * mm, "end": v(22.41, 68.15) * mm});
            skLineSegment(sketch, "E842", {"start": v(22.41, 68.15) * mm, "end": v(22.17, 68.75) * mm});
            skLineSegment(sketch, "E843", {"start": v(22.17, 68.75) * mm, "end": v(21.77, 69.27) * mm});
            skLineSegment(sketch, "E844", {"start": v(21.77, 69.27) * mm, "end": v(21.25, 69.67) * mm});
            skLineSegment(sketch, "E845", {"start": v(21.25, 69.67) * mm, "end": v(20.65, 69.91) * mm});
            skLineSegment(sketch, "E846", {"start": v(20.65, 69.91) * mm, "end": v(20, 70) * mm});
            skLineSegment(sketch, "E847", {"start": v(20, 70) * mm, "end": v(19.35, 69.91) * mm});
            skLineSegment(sketch, "E848", {"start": v(19.35, 69.91) * mm, "end": v(18.75, 69.67) * mm});
            skLineSegment(sketch, "E849", {"start": v(18.75, 69.67) * mm, "end": v(18.23, 69.27) * mm});
            skLineSegment(sketch, "E850", {"start": v(18.23, 69.27) * mm, "end": v(17.83, 68.75) * mm});
            skLineSegment(sketch, "E851", {"start": v(17.83, 68.75) * mm, "end": v(17.59, 68.15) * mm});
            skLineSegment(sketch, "E852", {"start": v(17.59, 68.15) * mm, "end": v(17.5, 67.5) * mm});
            skLineSegment(sketch, "E853", {"start": v(17.5, 67.5) * mm, "end": v(17.59, 66.85) * mm});
            skLineSegment(sketch, "E854", {"start": v(17.59, 66.85) * mm, "end": v(17.83, 66.25) * mm});
            skLineSegment(sketch, "E855", {"start": v(17.83, 66.25) * mm, "end": v(18.23, 65.73) * mm});
            skLineSegment(sketch, "E856", {"start": v(18.23, 65.73) * mm, "end": v(18.75, 65.33) * mm});
            skLineSegment(sketch, "E857", {"start": v(18.75, 65.33) * mm, "end": v(19.35, 65.09) * mm});
            skLineSegment(sketch, "E858", {"start": v(19.35, 65.09) * mm, "end": v(20, 65) * mm});
            skLineSegment(sketch, "E859", {"start": v(20, 65) * mm, "end": v(20.65, 65.09) * mm});
            skLineSegment(sketch, "E860", {"start": v(-20.65, 65.09) * mm, "end": v(-20, 65) * mm});
            skLineSegment(sketch, "E861", {"start": v(-20, 65) * mm, "end": v(-19.35, 65.09) * mm});
            skLineSegment(sketch, "E862", {"start": v(-19.35, 65.09) * mm, "end": v(-18.75, 65.33) * mm});
            skLineSegment(sketch, "E863", {"start": v(-18.75, 65.33) * mm, "end": v(-18.23, 65.73) * mm});
            skLineSegment(sketch, "E864", {"start": v(-18.23, 65.73) * mm, "end": v(-17.83, 66.25) * mm});
            skLineSegment(sketch, "E865", {"start": v(-17.83, 66.25) * mm, "end": v(-17.59, 66.85) * mm});
            skLineSegment(sketch, "E866", {"start": v(-17.59, 66.85) * mm, "end": v(-17.5, 67.5) * mm});
            skLineSegment(sketch, "E867", {"start": v(-17.5, 67.5) * mm, "end": v(-17.59, 68.15) * mm});
            skLineSegment(sketch, "E868", {"start": v(-17.59, 68.15) * mm, "end": v(-17.83, 68.75) * mm});
            skLineSegment(sketch, "E869", {"start": v(-17.83, 68.75) * mm, "end": v(-18.23, 69.27) * mm});
            skLineSegment(sketch, "E870", {"start": v(-18.23, 69.27) * mm, "end": v(-18.75, 69.67) * mm});
            skLineSegment(sketch, "E871", {"start": v(-18.75, 69.67) * mm, "end": v(-19.35, 69.91) * mm});
            skLineSegment(sketch, "E872", {"start": v(-19.35, 69.91) * mm, "end": v(-20, 70) * mm});
            skLineSegment(sketch, "E873", {"start": v(-20, 70) * mm, "end": v(-20.65, 69.91) * mm});
            skLineSegment(sketch, "E874", {"start": v(-20.65, 69.91) * mm, "end": v(-21.25, 69.67) * mm});
            skLineSegment(sketch, "E875", {"start": v(-21.25, 69.67) * mm, "end": v(-21.77, 69.27) * mm});
            skLineSegment(sketch, "E876", {"start": v(-21.77, 69.27) * mm, "end": v(-22.17, 68.75) * mm});
            skLineSegment(sketch, "E877", {"start": v(-22.17, 68.75) * mm, "end": v(-22.41, 68.15) * mm});
            skLineSegment(sketch, "E878", {"start": v(-22.41, 68.15) * mm, "end": v(-22.5, 67.5) * mm});
            skLineSegment(sketch, "E879", {"start": v(-22.5, 67.5) * mm, "end": v(-22.41, 66.85) * mm});
            skLineSegment(sketch, "E880", {"start": v(-22.41, 66.85) * mm, "end": v(-22.17, 66.25) * mm});
            skLineSegment(sketch, "E881", {"start": v(-22.17, 66.25) * mm, "end": v(-21.77, 65.73) * mm});
            skLineSegment(sketch, "E882", {"start": v(-21.77, 65.73) * mm, "end": v(-21.25, 65.33) * mm});
            skLineSegment(sketch, "E883", {"start": v(-21.25, 65.33) * mm, "end": v(-20.65, 65.09) * mm});
            skLineSegment(sketch, "E884", {"start": v(-57.59, 68.15) * mm, "end": v(-57.83, 68.75) * mm});
            skLineSegment(sketch, "E885", {"start": v(-57.83, 68.75) * mm, "end": v(-58.23, 69.27) * mm});
            skLineSegment(sketch, "E886", {"start": v(-58.23, 69.27) * mm, "end": v(-58.75, 69.67) * mm});
            skLineSegment(sketch, "E887", {"start": v(-58.75, 69.67) * mm, "end": v(-59.35, 69.91) * mm});
            skLineSegment(sketch, "E888", {"start": v(-59.35, 69.91) * mm, "end": v(-60, 70) * mm});
            skLineSegment(sketch, "E889", {"start": v(-60, 70) * mm, "end": v(-60.65, 69.91) * mm});
            skLineSegment(sketch, "E890", {"start": v(-60.65, 69.91) * mm, "end": v(-61.25, 69.67) * mm});
            skLineSegment(sketch, "E891", {"start": v(-61.25, 69.67) * mm, "end": v(-61.77, 69.27) * mm});
            skLineSegment(sketch, "E892", {"start": v(-61.77, 69.27) * mm, "end": v(-62.17, 68.75) * mm});
            skLineSegment(sketch, "E893", {"start": v(-62.17, 68.75) * mm, "end": v(-62.41, 68.15) * mm});
            skLineSegment(sketch, "E894", {"start": v(-62.41, 68.15) * mm, "end": v(-62.5, 67.5) * mm});
            skLineSegment(sketch, "E895", {"start": v(-62.5, 67.5) * mm, "end": v(-62.41, 66.85) * mm});
            skLineSegment(sketch, "E896", {"start": v(-62.41, 66.85) * mm, "end": v(-62.17, 66.25) * mm});
            skLineSegment(sketch, "E897", {"start": v(-62.17, 66.25) * mm, "end": v(-61.77, 65.73) * mm});
            skLineSegment(sketch, "E898", {"start": v(-61.77, 65.73) * mm, "end": v(-61.25, 65.33) * mm});
            skLineSegment(sketch, "E899", {"start": v(-61.25, 65.33) * mm, "end": v(-60.65, 65.09) * mm});
            skLineSegment(sketch, "E900", {"start": v(-60.65, 65.09) * mm, "end": v(-60, 65) * mm});
            skLineSegment(sketch, "E901", {"start": v(-60, 65) * mm, "end": v(-59.35, 65.09) * mm});
            skLineSegment(sketch, "E902", {"start": v(-59.35, 65.09) * mm, "end": v(-58.75, 65.33) * mm});
            skLineSegment(sketch, "E903", {"start": v(-58.75, 65.33) * mm, "end": v(-58.23, 65.73) * mm});
            skLineSegment(sketch, "E904", {"start": v(-58.23, 65.73) * mm, "end": v(-57.83, 66.25) * mm});
            skLineSegment(sketch, "E905", {"start": v(-57.83, 66.25) * mm, "end": v(-57.59, 66.85) * mm});
            skLineSegment(sketch, "E906", {"start": v(-57.59, 66.85) * mm, "end": v(-57.5, 67.5) * mm});
            skLineSegment(sketch, "E907", {"start": v(-57.5, 67.5) * mm, "end": v(-57.59, 68.15) * mm});
            skLineSegment(sketch, "E908", {"start": v(-101.77, -69.27) * mm, "end": v(-101.25, -69.67) * mm});
            skLineSegment(sketch, "E909", {"start": v(-101.25, -69.67) * mm, "end": v(-100.65, -69.91) * mm});
            skLineSegment(sketch, "E910", {"start": v(-100.65, -69.91) * mm, "end": v(-100, -70) * mm});
            skLineSegment(sketch, "E911", {"start": v(-100, -70) * mm, "end": v(-99.35, -69.91) * mm});
            skLineSegment(sketch, "E912", {"start": v(-99.35, -69.91) * mm, "end": v(-98.75, -69.67) * mm});
            skLineSegment(sketch, "E913", {"start": v(-98.75, -69.67) * mm, "end": v(-98.23, -69.27) * mm});
            skLineSegment(sketch, "E914", {"start": v(-98.23, -69.27) * mm, "end": v(-97.83, -68.75) * mm});
            skLineSegment(sketch, "E915", {"start": v(-97.83, -68.75) * mm, "end": v(-97.59, -68.15) * mm});
            skLineSegment(sketch, "E916", {"start": v(-97.59, -68.15) * mm, "end": v(-97.5, -67.5) * mm});
            skLineSegment(sketch, "E917", {"start": v(-97.5, -67.5) * mm, "end": v(-97.59, -66.85) * mm});
            skLineSegment(sketch, "E918", {"start": v(-97.59, -66.85) * mm, "end": v(-97.83, -66.25) * mm});
            skLineSegment(sketch, "E919", {"start": v(-97.83, -66.25) * mm, "end": v(-98.23, -65.73) * mm});
            skLineSegment(sketch, "E920", {"start": v(-98.23, -65.73) * mm, "end": v(-98.75, -65.33) * mm});
            skLineSegment(sketch, "E921", {"start": v(-98.75, -65.33) * mm, "end": v(-99.35, -65.09) * mm});
            skLineSegment(sketch, "E922", {"start": v(-99.35, -65.09) * mm, "end": v(-100, -65) * mm});
            skLineSegment(sketch, "E923", {"start": v(-100, -65) * mm, "end": v(-100.65, -65.09) * mm});
            skLineSegment(sketch, "E924", {"start": v(-100.65, -65.09) * mm, "end": v(-101.25, -65.33) * mm});
            skLineSegment(sketch, "E925", {"start": v(-101.25, -65.33) * mm, "end": v(-101.77, -65.73) * mm});
            skLineSegment(sketch, "E926", {"start": v(-101.77, -65.73) * mm, "end": v(-102.17, -66.25) * mm});
            skLineSegment(sketch, "E927", {"start": v(-102.17, -66.25) * mm, "end": v(-102.41, -66.85) * mm});
            skLineSegment(sketch, "E928", {"start": v(-102.41, -66.85) * mm, "end": v(-102.5, -67.5) * mm});
            skLineSegment(sketch, "E929", {"start": v(-102.5, -67.5) * mm, "end": v(-102.41, -68.15) * mm});
            skLineSegment(sketch, "E930", {"start": v(-102.41, -68.15) * mm, "end": v(-102.17, -68.75) * mm});
            skLineSegment(sketch, "E931", {"start": v(-102.17, -68.75) * mm, "end": v(-101.77, -69.27) * mm});
            skLineSegment(sketch, "E932", {"start": v(-60.65, -65.09) * mm, "end": v(-61.25, -65.33) * mm});
            skLineSegment(sketch, "E933", {"start": v(-61.25, -65.33) * mm, "end": v(-61.77, -65.73) * mm});
            skLineSegment(sketch, "E934", {"start": v(-61.77, -65.73) * mm, "end": v(-62.17, -66.25) * mm});
            skLineSegment(sketch, "E935", {"start": v(-62.17, -66.25) * mm, "end": v(-62.41, -66.85) * mm});
            skLineSegment(sketch, "E936", {"start": v(-62.41, -66.85) * mm, "end": v(-62.5, -67.5) * mm});
            skLineSegment(sketch, "E937", {"start": v(-62.5, -67.5) * mm, "end": v(-62.41, -68.15) * mm});
            skLineSegment(sketch, "E938", {"start": v(-62.41, -68.15) * mm, "end": v(-62.17, -68.75) * mm});
            skLineSegment(sketch, "E939", {"start": v(-62.17, -68.75) * mm, "end": v(-61.77, -69.27) * mm});
            skLineSegment(sketch, "E940", {"start": v(-61.77, -69.27) * mm, "end": v(-61.25, -69.67) * mm});
            skLineSegment(sketch, "E941", {"start": v(-61.25, -69.67) * mm, "end": v(-60.65, -69.91) * mm});
            skLineSegment(sketch, "E942", {"start": v(-60.65, -69.91) * mm, "end": v(-60, -70) * mm});
            skLineSegment(sketch, "E943", {"start": v(-60, -70) * mm, "end": v(-59.35, -69.91) * mm});
            skLineSegment(sketch, "E944", {"start": v(-59.35, -69.91) * mm, "end": v(-58.75, -69.67) * mm});
            skLineSegment(sketch, "E945", {"start": v(-58.75, -69.67) * mm, "end": v(-58.23, -69.27) * mm});
            skLineSegment(sketch, "E946", {"start": v(-58.23, -69.27) * mm, "end": v(-57.83, -68.75) * mm});
            skLineSegment(sketch, "E947", {"start": v(-57.83, -68.75) * mm, "end": v(-57.59, -68.15) * mm});
            skLineSegment(sketch, "E948", {"start": v(-57.59, -68.15) * mm, "end": v(-57.5, -67.5) * mm});
            skLineSegment(sketch, "E949", {"start": v(-57.5, -67.5) * mm, "end": v(-57.59, -66.85) * mm});
            skLineSegment(sketch, "E950", {"start": v(-57.59, -66.85) * mm, "end": v(-57.83, -66.25) * mm});
            skLineSegment(sketch, "E951", {"start": v(-57.83, -66.25) * mm, "end": v(-58.23, -65.73) * mm});
            skLineSegment(sketch, "E952", {"start": v(-58.23, -65.73) * mm, "end": v(-58.75, -65.33) * mm});
            skLineSegment(sketch, "E953", {"start": v(-58.75, -65.33) * mm, "end": v(-59.35, -65.09) * mm});
            skLineSegment(sketch, "E954", {"start": v(-59.35, -65.09) * mm, "end": v(-60, -65) * mm});
            skLineSegment(sketch, "E955", {"start": v(-60, -65) * mm, "end": v(-60.65, -65.09) * mm});
            skLineSegment(sketch, "E956", {"start": v(-17.83, -66.25) * mm, "end": v(-18.23, -65.73) * mm});
            skLineSegment(sketch, "E957", {"start": v(-18.23, -65.73) * mm, "end": v(-18.75, -65.33) * mm});
            skLineSegment(sketch, "E958", {"start": v(-18.75, -65.33) * mm, "end": v(-19.35, -65.09) * mm});
            skLineSegment(sketch, "E959", {"start": v(-19.35, -65.09) * mm, "end": v(-20, -65) * mm});
            skLineSegment(sketch, "E960", {"start": v(-20, -65) * mm, "end": v(-20.65, -65.09) * mm});
            skLineSegment(sketch, "E961", {"start": v(-20.65, -65.09) * mm, "end": v(-21.25, -65.33) * mm});
            skLineSegment(sketch, "E962", {"start": v(-21.25, -65.33) * mm, "end": v(-21.77, -65.73) * mm});
            skLineSegment(sketch, "E963", {"start": v(-21.77, -65.73) * mm, "end": v(-22.17, -66.25) * mm});
            skLineSegment(sketch, "E964", {"start": v(-22.17, -66.25) * mm, "end": v(-22.41, -66.85) * mm});
            skLineSegment(sketch, "E965", {"start": v(-22.41, -66.85) * mm, "end": v(-22.5, -67.5) * mm});
            skLineSegment(sketch, "E966", {"start": v(-22.5, -67.5) * mm, "end": v(-22.41, -68.15) * mm});
            skLineSegment(sketch, "E967", {"start": v(-22.41, -68.15) * mm, "end": v(-22.17, -68.75) * mm});
            skLineSegment(sketch, "E968", {"start": v(-22.17, -68.75) * mm, "end": v(-21.77, -69.27) * mm});
            skLineSegment(sketch, "E969", {"start": v(-21.77, -69.27) * mm, "end": v(-21.25, -69.67) * mm});
            skLineSegment(sketch, "E970", {"start": v(-21.25, -69.67) * mm, "end": v(-20.65, -69.91) * mm});
            skLineSegment(sketch, "E971", {"start": v(-20.65, -69.91) * mm, "end": v(-20, -70) * mm});
            skLineSegment(sketch, "E972", {"start": v(-20, -70) * mm, "end": v(-19.35, -69.91) * mm});
            skLineSegment(sketch, "E973", {"start": v(-19.35, -69.91) * mm, "end": v(-18.75, -69.67) * mm});
            skLineSegment(sketch, "E974", {"start": v(-18.75, -69.67) * mm, "end": v(-18.23, -69.27) * mm});
            skLineSegment(sketch, "E975", {"start": v(-18.23, -69.27) * mm, "end": v(-17.83, -68.75) * mm});
            skLineSegment(sketch, "E976", {"start": v(-17.83, -68.75) * mm, "end": v(-17.59, -68.15) * mm});
            skLineSegment(sketch, "E977", {"start": v(-17.59, -68.15) * mm, "end": v(-17.5, -67.5) * mm});
            skLineSegment(sketch, "E978", {"start": v(-17.5, -67.5) * mm, "end": v(-17.59, -66.85) * mm});
            skLineSegment(sketch, "E979", {"start": v(-17.59, -66.85) * mm, "end": v(-17.83, -66.25) * mm});
            skLineSegment(sketch, "E980", {"start": v(18.23, -65.73) * mm, "end": v(17.83, -66.25) * mm});
            skLineSegment(sketch, "E981", {"start": v(17.83, -66.25) * mm, "end": v(17.59, -66.85) * mm});
            skLineSegment(sketch, "E982", {"start": v(17.59, -66.85) * mm, "end": v(17.5, -67.5) * mm});
            skLineSegment(sketch, "E983", {"start": v(17.5, -67.5) * mm, "end": v(17.59, -68.15) * mm});
            skLineSegment(sketch, "E984", {"start": v(17.59, -68.15) * mm, "end": v(17.83, -68.75) * mm});
            skLineSegment(sketch, "E985", {"start": v(17.83, -68.75) * mm, "end": v(18.23, -69.27) * mm});
            skLineSegment(sketch, "E986", {"start": v(18.23, -69.27) * mm, "end": v(18.75, -69.67) * mm});
            skLineSegment(sketch, "E987", {"start": v(18.75, -69.67) * mm, "end": v(19.35, -69.91) * mm});
            skLineSegment(sketch, "E988", {"start": v(19.35, -69.91) * mm, "end": v(20, -70) * mm});
            skLineSegment(sketch, "E989", {"start": v(20, -70) * mm, "end": v(20.65, -69.91) * mm});
            skLineSegment(sketch, "E990", {"start": v(20.65, -69.91) * mm, "end": v(21.25, -69.67) * mm});
            skLineSegment(sketch, "E991", {"start": v(21.25, -69.67) * mm, "end": v(21.77, -69.27) * mm});
            skLineSegment(sketch, "E992", {"start": v(21.77, -69.27) * mm, "end": v(22.17, -68.75) * mm});
            skLineSegment(sketch, "E993", {"start": v(22.17, -68.75) * mm, "end": v(22.41, -68.15) * mm});
            skLineSegment(sketch, "E994", {"start": v(22.41, -68.15) * mm, "end": v(22.5, -67.5) * mm});
            skLineSegment(sketch, "E995", {"start": v(22.5, -67.5) * mm, "end": v(22.41, -66.85) * mm});
            skLineSegment(sketch, "E996", {"start": v(22.41, -66.85) * mm, "end": v(22.17, -66.25) * mm});
            skLineSegment(sketch, "E997", {"start": v(22.17, -66.25) * mm, "end": v(21.77, -65.73) * mm});
            skLineSegment(sketch, "E998", {"start": v(21.77, -65.73) * mm, "end": v(21.25, -65.33) * mm});
            skLineSegment(sketch, "E999", {"start": v(21.25, -65.33) * mm, "end": v(20.65, -65.09) * mm});
            skLineSegment(sketch, "E1000", {"start": v(20.65, -65.09) * mm, "end": v(20, -65) * mm});
            skLineSegment(sketch, "E1001", {"start": v(20, -65) * mm, "end": v(19.35, -65.09) * mm});
            skLineSegment(sketch, "E1002", {"start": v(19.35, -65.09) * mm, "end": v(18.75, -65.33) * mm});
            skLineSegment(sketch, "E1003", {"start": v(18.75, -65.33) * mm, "end": v(18.23, -65.73) * mm});
            skCircle(sketch, "E1004", {"center": v(-100, 67.5) * mm, "radius": 2.5 * mm});
            skSolve(sketch);
        }
        {
            var Q0;
            Q0 = qSketchRegion(id + "F0", true);
            extrude(context, id + "F1", {"entities" : qUnion([Q0]), "depth" : 15 * mm});
        }
        {
            var Q0;
            Q0=qCreatedBy(makeId("Right.planeOp"),FACE);
            var sketch = newSketch(context, id + "F2", { "sketchPlane" : qUnion([Q0])});
            skCircle(sketch, "E1005", {"center": v(-53.97, -27.13) * mm, "radius": 4 * mm});
            skSolve(sketch);
        }
        {
            var Q0;
            Q0=makeQuery(id+"F2.imprint","IMPRINT",FACE,{"disambiguationData":[TD([[makeQuery(id+"F2.imprint","IMPRINT",EDGE,{"derivedFrom":sQuery(id+"F2.wireOp",EDGE,"E1005")}),1.0]])]});
            extrude(context, id + "F3", {"entities" : qUnion([Q0]), "endBound" : BoundingType.SYMMETRIC, "depth" : 400 * mm});
        }
        {
            var Q0;
            Q0=makeQuery(id+"F3.opExtrude","SWEPT_BODY",BODY,{"disambiguationData":[OSD([sQuery(id+"F2.wireOp",EDGE,"E1005")])]});
            var Q1;
            Q1=qCreatedBy(makeId("Front.planeOp"),FACE);
            mirror(context, id + "F4", {"entities" : qUnion([Q0]), "mirrorPlane" : qUnion([Q1])});
        }
        {
            var Q0;
            Q0=qCreatedBy(makeId("Right.planeOp"),FACE);
            cPlane(context, id + "F5", {"entities" : qUnion([Q0]), "cplaneType" : CPlaneType.OFFSET, "offset" : 200 * mm, "width" : 150 * mm, "height" : 150 * mm});
        }
        {
            var Q0;
            Q0=qCreatedBy(id+"F5.planeOp",FACE);
            var sketch = newSketch(context, id + "F6", { "sketchPlane" : qUnion([Q0])});
            skLineSegment(sketch, "E1006", {"start": v(110, -20) * mm, "end": v(-110, -20) * mm});
            skLineSegment(sketch, "E1007", {"start": v(-110, -20) * mm, "end": v(-110, 10) * mm});
            skLineSegment(sketch, "E1008", {"start": v(-100, 20) * mm, "end": v(100, 20) * mm});
            skLineSegment(sketch, "E1009", {"start": v(110, 10) * mm, "end": v(110, -20) * mm});
            skCircle(sketch, "E1010", {"center": v(-85, 0) * mm, "radius": 7.5 * mm});
            skCircle(sketch, "E1011", {"center": v(0, 0) * mm, "radius": 4.5 * mm});
            skCircle(sketch, "E1012", {"center": v(85, 0) * mm, "radius": 7.5 * mm});
            skArc(sketch, "E1013", {"start": v(-110, 10) * mm, "mid": v(-107.07, 17.07) * mm, "end": v(-100, 20) * mm});
            skArc(sketch, "E1014", {"start": v(100, 20) * mm, "mid": v(107.07, 17.07) * mm, "end": v(110, 10) * mm});
            skSolve(sketch);
        }
        {
            var Q0;
            Q0=makeQuery(id+"F6.imprint","IMPRINT",FACE,{"disambiguationData":[TD([[makeQuery(id+"F6.imprint","IMPRINT",EDGE,{"derivedFrom":sQuery(id+"F6.wireOp",EDGE,"E1006")}),-1.0]])]});
            extrude(context, id + "F7", {"entities" : qUnion([Q0]), "depth" : 15 * mm});
        }
        {
            var Q0;
            Q0=qCreatedBy(makeId("Right.planeOp"),FACE);
            cPlane(context, id + "F8", {"entities" : qUnion([Q0]), "cplaneType" : CPlaneType.OFFSET, "offset" : 200 * mm, "oppositeDirection" : true, "width" : 150 * mm, "height" : 150 * mm});
        }
        {
            var Q0;
            Q0=qCreatedBy(id+"F8.planeOp",FACE);
            var sketch = newSketch(context, id + "F9", { "sketchPlane" : qUnion([Q0])});
            skLineSegment(sketch, "E1015", {"start": v(110, -20) * mm, "end": v(-110, -20) * mm});
            skLineSegment(sketch, "E1016", {"start": v(-110, -20) * mm, "end": v(-110, 10) * mm});
            skLineSegment(sketch, "E1017", {"start": v(-110, 10) * mm, "end": v(-109.91, 11.3) * mm});
            skLineSegment(sketch, "E1018", {"start": v(-109.91, 11.3) * mm, "end": v(-109.66, 12.59) * mm});
            skLineSegment(sketch, "E1019", {"start": v(-109.66, 12.59) * mm, "end": v(-109.24, 13.83) * mm});
            skLineSegment(sketch, "E1020", {"start": v(-109.24, 13.83) * mm, "end": v(-108.66, 15) * mm});
            skLineSegment(sketch, "E1021", {"start": v(-108.66, 15) * mm, "end": v(-107.93, 16.09) * mm});
            skLineSegment(sketch, "E1022", {"start": v(-107.93, 16.09) * mm, "end": v(-107.07, 17.07) * mm});
            skLineSegment(sketch, "E1023", {"start": v(-107.07, 17.07) * mm, "end": v(-106.09, 17.93) * mm});
            skLineSegment(sketch, "E1024", {"start": v(-106.09, 17.93) * mm, "end": v(-105, 18.66) * mm});
            skLineSegment(sketch, "E1025", {"start": v(-105, 18.66) * mm, "end": v(-103.83, 19.24) * mm});
            skLineSegment(sketch, "E1026", {"start": v(-103.83, 19.24) * mm, "end": v(-102.59, 19.66) * mm});
            skLineSegment(sketch, "E1027", {"start": v(-102.59, 19.66) * mm, "end": v(-101.3, 19.91) * mm});
            skLineSegment(sketch, "E1028", {"start": v(-101.3, 19.91) * mm, "end": v(-100, 20) * mm});
            skLineSegment(sketch, "E1029", {"start": v(-100, 20) * mm, "end": v(100, 20) * mm});
            skLineSegment(sketch, "E1030", {"start": v(100, 20) * mm, "end": v(101.3, 19.91) * mm});
            skLineSegment(sketch, "E1031", {"start": v(101.3, 19.91) * mm, "end": v(102.59, 19.66) * mm});
            skLineSegment(sketch, "E1032", {"start": v(102.59, 19.66) * mm, "end": v(103.83, 19.24) * mm});
            skLineSegment(sketch, "E1033", {"start": v(103.83, 19.24) * mm, "end": v(105, 18.66) * mm});
            skLineSegment(sketch, "E1034", {"start": v(105, 18.66) * mm, "end": v(106.09, 17.93) * mm});
            skLineSegment(sketch, "E1035", {"start": v(106.09, 17.93) * mm, "end": v(107.07, 17.07) * mm});
            skLineSegment(sketch, "E1036", {"start": v(107.07, 17.07) * mm, "end": v(107.93, 16.09) * mm});
            skLineSegment(sketch, "E1037", {"start": v(107.93, 16.09) * mm, "end": v(108.66, 15) * mm});
            skLineSegment(sketch, "E1038", {"start": v(108.66, 15) * mm, "end": v(109.24, 13.83) * mm});
            skLineSegment(sketch, "E1039", {"start": v(109.24, 13.83) * mm, "end": v(109.66, 12.59) * mm});
            skLineSegment(sketch, "E1040", {"start": v(109.66, 12.59) * mm, "end": v(109.91, 11.3) * mm});
            skLineSegment(sketch, "E1041", {"start": v(109.91, 11.3) * mm, "end": v(110, 10) * mm});
            skLineSegment(sketch, "E1042", {"start": v(110, 10) * mm, "end": v(110, -20) * mm});
            skLineSegment(sketch, "E1043", {"start": v(20.92, 1.18) * mm, "end": v(20.58, 1.38) * mm});
            skLineSegment(sketch, "E1044", {"start": v(20.58, 1.38) * mm, "end": v(20.2, 1.49) * mm});
            skLineSegment(sketch, "E1045", {"start": v(20.2, 1.49) * mm, "end": v(19.81, 1.49) * mm});
            skLineSegment(sketch, "E1046", {"start": v(19.81, 1.49) * mm, "end": v(19.43, 1.39) * mm});
            skLineSegment(sketch, "E1047", {"start": v(19.43, 1.39) * mm, "end": v(19.1, 1.2) * mm});
            skLineSegment(sketch, "E1048", {"start": v(19.1, 1.2) * mm, "end": v(18.82, 0.92) * mm});
            skLineSegment(sketch, "E1049", {"start": v(18.82, 0.92) * mm, "end": v(18.62, 0.58) * mm});
            skLineSegment(sketch, "E1050", {"start": v(18.62, 0.58) * mm, "end": v(18.51, 0.2) * mm});
            skLineSegment(sketch, "E1051", {"start": v(18.51, 0.2) * mm, "end": v(18.51, -0.19) * mm});
            skLineSegment(sketch, "E1052", {"start": v(18.51, -0.19) * mm, "end": v(18.61, -0.57) * mm});
            skLineSegment(sketch, "E1053", {"start": v(18.61, -0.57) * mm, "end": v(18.8, -0.9) * mm});
            skLineSegment(sketch, "E1054", {"start": v(18.8, -0.9) * mm, "end": v(19.08, -1.18) * mm});
            skLineSegment(sketch, "E1055", {"start": v(19.08, -1.18) * mm, "end": v(19.42, -1.38) * mm});
            skLineSegment(sketch, "E1056", {"start": v(19.42, -1.38) * mm, "end": v(19.8, -1.49) * mm});
            skLineSegment(sketch, "E1057", {"start": v(19.8, -1.49) * mm, "end": v(20.19, -1.49) * mm});
            skLineSegment(sketch, "E1058", {"start": v(20.19, -1.49) * mm, "end": v(20.57, -1.39) * mm});
            skLineSegment(sketch, "E1059", {"start": v(20.57, -1.39) * mm, "end": v(20.9, -1.2) * mm});
            skLineSegment(sketch, "E1060", {"start": v(20.9, -1.2) * mm, "end": v(21.18, -0.92) * mm});
            skLineSegment(sketch, "E1061", {"start": v(21.18, -0.92) * mm, "end": v(21.38, -0.58) * mm});
            skLineSegment(sketch, "E1062", {"start": v(21.38, -0.58) * mm, "end": v(21.49, -0.2) * mm});
            skLineSegment(sketch, "E1063", {"start": v(21.49, -0.2) * mm, "end": v(21.49, 0.19) * mm});
            skLineSegment(sketch, "E1064", {"start": v(21.49, 0.19) * mm, "end": v(21.39, 0.57) * mm});
            skLineSegment(sketch, "E1065", {"start": v(21.39, 0.57) * mm, "end": v(21.2, 0.9) * mm});
            skLineSegment(sketch, "E1066", {"start": v(21.2, 0.9) * mm, "end": v(20.92, 1.18) * mm});
            skLineSegment(sketch, "E1067", {"start": v(-21.3, 0.75) * mm, "end": v(-21.45, 0.39) * mm});
            skLineSegment(sketch, "E1068", {"start": v(-21.45, 0.39) * mm, "end": v(-21.5, 0) * mm});
            skLineSegment(sketch, "E1069", {"start": v(-21.5, 0) * mm, "end": v(-21.45, -0.39) * mm});
            skLineSegment(sketch, "E1070", {"start": v(-21.45, -0.39) * mm, "end": v(-21.3, -0.75) * mm});
            skLineSegment(sketch, "E1071", {"start": v(-21.3, -0.75) * mm, "end": v(-21.06, -1.06) * mm});
            skLineSegment(sketch, "E1072", {"start": v(-21.06, -1.06) * mm, "end": v(-20.75, -1.3) * mm});
            skLineSegment(sketch, "E1073", {"start": v(-20.75, -1.3) * mm, "end": v(-20.39, -1.45) * mm});
            skLineSegment(sketch, "E1074", {"start": v(-20.39, -1.45) * mm, "end": v(-20, -1.5) * mm});
            skLineSegment(sketch, "E1075", {"start": v(-20, -1.5) * mm, "end": v(-19.61, -1.45) * mm});
            skLineSegment(sketch, "E1076", {"start": v(-19.61, -1.45) * mm, "end": v(-19.25, -1.3) * mm});
            skLineSegment(sketch, "E1077", {"start": v(-19.25, -1.3) * mm, "end": v(-18.94, -1.06) * mm});
            skLineSegment(sketch, "E1078", {"start": v(-18.94, -1.06) * mm, "end": v(-18.7, -0.75) * mm});
            skLineSegment(sketch, "E1079", {"start": v(-18.7, -0.75) * mm, "end": v(-18.55, -0.39) * mm});
            skLineSegment(sketch, "E1080", {"start": v(-18.55, -0.39) * mm, "end": v(-18.5, 0) * mm});
            skLineSegment(sketch, "E1081", {"start": v(-18.5, 0) * mm, "end": v(-18.55, 0.39) * mm});
            skLineSegment(sketch, "E1082", {"start": v(-18.55, 0.39) * mm, "end": v(-18.7, 0.75) * mm});
            skLineSegment(sketch, "E1083", {"start": v(-18.7, 0.75) * mm, "end": v(-18.94, 1.06) * mm});
            skLineSegment(sketch, "E1084", {"start": v(-18.94, 1.06) * mm, "end": v(-19.25, 1.3) * mm});
            skLineSegment(sketch, "E1085", {"start": v(-19.25, 1.3) * mm, "end": v(-19.61, 1.45) * mm});
            skLineSegment(sketch, "E1086", {"start": v(-19.61, 1.45) * mm, "end": v(-20, 1.5) * mm});
            skLineSegment(sketch, "E1087", {"start": v(-20, 1.5) * mm, "end": v(-20.39, 1.45) * mm});
            skLineSegment(sketch, "E1088", {"start": v(-20.39, 1.45) * mm, "end": v(-20.75, 1.3) * mm});
            skLineSegment(sketch, "E1089", {"start": v(-20.75, 1.3) * mm, "end": v(-21.06, 1.06) * mm});
            skLineSegment(sketch, "E1090", {"start": v(-21.06, 1.06) * mm, "end": v(-21.3, 0.75) * mm});
            skCircle(sketch, "E1091", {"center": v(85, 0) * mm, "radius": 7.5 * mm});
            skCircle(sketch, "E1092", {"center": v(0.02, 0.05) * mm, "radius": 9.97 * mm});
            skCircle(sketch, "E1093", {"center": v(-85, 0) * mm, "radius": 7.5 * mm});
            skSolve(sketch);
        }
        {
            var Q0;
            Q0=makeQuery(id+"F9.imprint","IMPRINT",FACE,{"disambiguationData":[TD([[makeQuery(id+"F9.imprint","IMPRINT",EDGE,{"derivedFrom":sQuery(id+"F9.wireOp",EDGE,"E1015")}),-1.0]])]});
            extrude(context, id + "F10", {"entities" : qUnion([Q0]), "depth" : 15 * mm});
        }
    });
